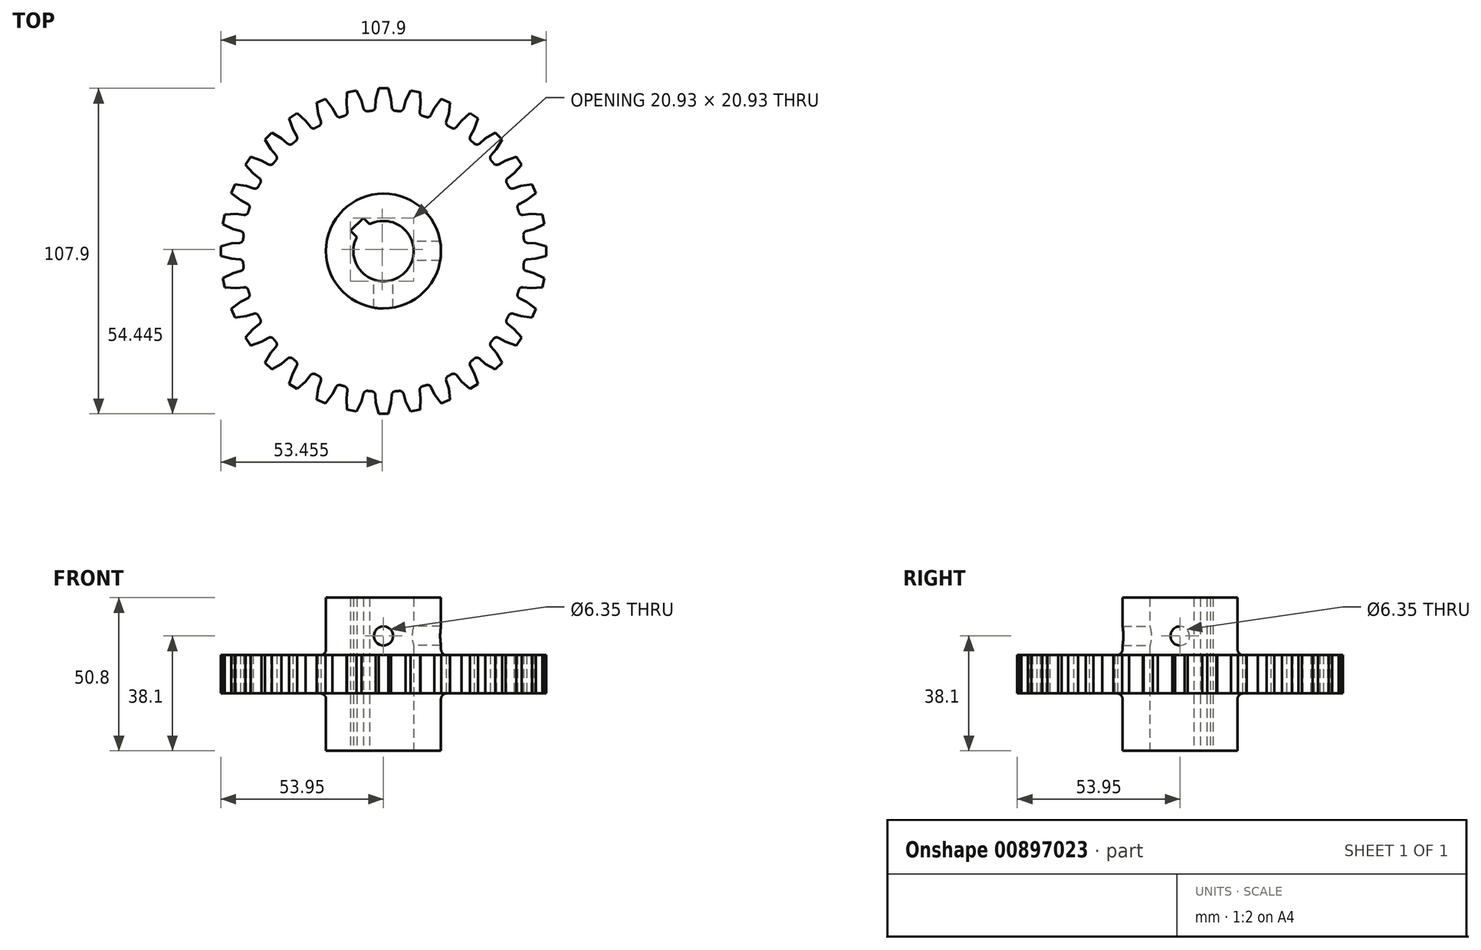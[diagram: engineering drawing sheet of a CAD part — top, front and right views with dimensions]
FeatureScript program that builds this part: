
annotation { "Feature Type Name" : "Feature", "Feature Type Description" : "" }
export const myFeature = defineFeature(function(context is Context, id is Id, definition is map)
    precondition{}
    {
        {
            var Q0;
            Q0=qCreatedBy(makeId("Top.planeOp"),FACE);
            var sketch = newSketch(context, id + "F0", { "sketchPlane" : qUnion([Q0])});
            skArc(sketch, "E0", {"start": v(-2.82, 46.59) * mm, "mid": v(-4.57, 46.45) * mm, "end": v(-6.32, 46.24) * mm});
            skLineSegment(sketch, "E1", {"start": v(1.59, 53.95) * mm, "end": v(-1.59, 53.95) * mm});
            skPoint(sketch, "E2", {"position": v(0, 53.95) * mm});
            skLineSegment(sketch, "E3", {"start": v(-1.59, 53.95) * mm, "end": v(-2.54, 50.31) * mm});
            skLineSegment(sketch, "E4", {"start": v(1.59, 53.95) * mm, "end": v(2.54, 50.31) * mm});
            skLineSegment(sketch, "E5", {"start": v(-2.54, 50.31) * mm, "end": v(-2.82, 46.59) * mm});
            skLineSegment(sketch, "E6", {"start": v(2.54, 50.31) * mm, "end": v(2.82, 46.59) * mm});
            skLineSegment(sketch, "E7.1.0", {"start": v(-8.97, 53.22) * mm, "end": v(-12.08, 52.6) * mm});
            skLineSegment(sketch, "E7.1.1", {"start": v(-7.32, 49.84) * mm, "end": v(-6.32, 46.24) * mm});
            skLineSegment(sketch, "E7.1.2", {"start": v(-8.97, 53.22) * mm, "end": v(-7.32, 49.84) * mm});
            skLineSegment(sketch, "E7.1.3", {"start": v(-12.08, 52.6) * mm, "end": v(-12.3, 48.85) * mm});
            skLineSegment(sketch, "E7.1.4", {"start": v(-12.3, 48.85) * mm, "end": v(-11.86, 45.14) * mm});
            skPoint(sketch, "E7.1.5", {"position": v(-10.53, 52.91) * mm});
            skLineSegment(sketch, "E7.2.0", {"start": v(-19.18, 50.45) * mm, "end": v(-22.11, 49.24) * mm});
            skLineSegment(sketch, "E7.2.1", {"start": v(-16.9, 47.45) * mm, "end": v(-15.22, 44.12) * mm});
            skLineSegment(sketch, "E7.2.2", {"start": v(-19.18, 50.45) * mm, "end": v(-16.9, 47.45) * mm});
            skLineSegment(sketch, "E7.2.3", {"start": v(-22.11, 49.24) * mm, "end": v(-21.6, 45.51) * mm});
            skLineSegment(sketch, "E7.2.4", {"start": v(-21.6, 45.51) * mm, "end": v(-20.44, 41.96) * mm});
            skPoint(sketch, "E7.2.5", {"position": v(-20.65, 49.84) * mm});
            skLineSegment(sketch, "E7.3.0", {"start": v(-28.65, 45.74) * mm, "end": v(-31.3, 43.98) * mm});
            skLineSegment(sketch, "E7.3.1", {"start": v(-25.84, 43.24) * mm, "end": v(-23.54, 40.3) * mm});
            skLineSegment(sketch, "E7.3.2", {"start": v(-28.65, 45.74) * mm, "end": v(-25.84, 43.24) * mm});
            skLineSegment(sketch, "E7.3.3", {"start": v(-31.3, 43.98) * mm, "end": v(-30.06, 40.42) * mm});
            skLineSegment(sketch, "E7.3.4", {"start": v(-30.06, 40.42) * mm, "end": v(-28.23, 37.17) * mm});
            skPoint(sketch, "E7.3.5", {"position": v(-29.97, 44.86) * mm});
            skLineSegment(sketch, "E7.4.0", {"start": v(-37.03, 39.27) * mm, "end": v(-39.27, 37.03) * mm});
            skLineSegment(sketch, "E7.4.1", {"start": v(-33.78, 37.37) * mm, "end": v(-30.95, 34.94) * mm});
            skLineSegment(sketch, "E7.4.2", {"start": v(-37.03, 39.27) * mm, "end": v(-33.78, 37.37) * mm});
            skLineSegment(sketch, "E7.4.3", {"start": v(-39.27, 37.03) * mm, "end": v(-37.37, 33.78) * mm});
            skLineSegment(sketch, "E7.4.4", {"start": v(-37.37, 33.78) * mm, "end": v(-34.94, 30.95) * mm});
            skPoint(sketch, "E7.4.5", {"position": v(-38.15, 38.15) * mm});
            skLineSegment(sketch, "E7.5.0", {"start": v(-43.98, 31.3) * mm, "end": v(-45.74, 28.65) * mm});
            skLineSegment(sketch, "E7.5.1", {"start": v(-40.42, 30.06) * mm, "end": v(-37.17, 28.23) * mm});
            skLineSegment(sketch, "E7.5.2", {"start": v(-43.98, 31.3) * mm, "end": v(-40.42, 30.06) * mm});
            skLineSegment(sketch, "E7.5.3", {"start": v(-45.74, 28.65) * mm, "end": v(-43.24, 25.84) * mm});
            skLineSegment(sketch, "E7.5.4", {"start": v(-43.24, 25.84) * mm, "end": v(-40.3, 23.54) * mm});
            skPoint(sketch, "E7.5.5", {"position": v(-44.86, 29.97) * mm});
            skLineSegment(sketch, "E7.6.0", {"start": v(-49.24, 22.11) * mm, "end": v(-50.45, 19.18) * mm});
            skLineSegment(sketch, "E7.6.1", {"start": v(-45.51, 21.6) * mm, "end": v(-41.96, 20.44) * mm});
            skLineSegment(sketch, "E7.6.2", {"start": v(-49.24, 22.11) * mm, "end": v(-45.51, 21.6) * mm});
            skLineSegment(sketch, "E7.6.3", {"start": v(-50.45, 19.18) * mm, "end": v(-47.45, 16.9) * mm});
            skLineSegment(sketch, "E7.6.4", {"start": v(-47.45, 16.9) * mm, "end": v(-44.12, 15.22) * mm});
            skPoint(sketch, "E7.6.5", {"position": v(-49.84, 20.65) * mm});
            skLineSegment(sketch, "E7.7.0", {"start": v(-52.6, 12.08) * mm, "end": v(-53.22, 8.97) * mm});
            skLineSegment(sketch, "E7.7.1", {"start": v(-48.85, 12.3) * mm, "end": v(-45.14, 11.86) * mm});
            skLineSegment(sketch, "E7.7.2", {"start": v(-52.6, 12.08) * mm, "end": v(-48.85, 12.3) * mm});
            skLineSegment(sketch, "E7.7.3", {"start": v(-53.22, 8.97) * mm, "end": v(-49.84, 7.32) * mm});
            skLineSegment(sketch, "E7.7.4", {"start": v(-49.84, 7.32) * mm, "end": v(-46.24, 6.32) * mm});
            skPoint(sketch, "E7.7.5", {"position": v(-52.91, 10.53) * mm});
            skLineSegment(sketch, "E7.8.0", {"start": v(-53.95, 1.59) * mm, "end": v(-53.95, -1.59) * mm});
            skLineSegment(sketch, "E7.8.1", {"start": v(-50.31, 2.54) * mm, "end": v(-46.59, 2.82) * mm});
            skLineSegment(sketch, "E7.8.2", {"start": v(-53.95, 1.59) * mm, "end": v(-50.31, 2.54) * mm});
            skLineSegment(sketch, "E7.8.3", {"start": v(-53.95, -1.59) * mm, "end": v(-50.31, -2.54) * mm});
            skLineSegment(sketch, "E7.8.4", {"start": v(-50.31, -2.54) * mm, "end": v(-46.59, -2.82) * mm});
            skPoint(sketch, "E7.8.5", {"position": v(-53.95, 0) * mm});
            skLineSegment(sketch, "E7.9.0", {"start": v(-53.22, -8.97) * mm, "end": v(-52.6, -12.08) * mm});
            skLineSegment(sketch, "E7.9.1", {"start": v(-49.84, -7.32) * mm, "end": v(-46.24, -6.32) * mm});
            skLineSegment(sketch, "E7.9.2", {"start": v(-53.22, -8.97) * mm, "end": v(-49.84, -7.32) * mm});
            skLineSegment(sketch, "E7.9.3", {"start": v(-52.6, -12.08) * mm, "end": v(-48.85, -12.3) * mm});
            skLineSegment(sketch, "E7.9.4", {"start": v(-48.85, -12.3) * mm, "end": v(-45.14, -11.86) * mm});
            skPoint(sketch, "E7.9.5", {"position": v(-52.91, -10.53) * mm});
            skLineSegment(sketch, "E7.10.0", {"start": v(-50.45, -19.18) * mm, "end": v(-49.24, -22.11) * mm});
            skLineSegment(sketch, "E7.10.1", {"start": v(-47.45, -16.9) * mm, "end": v(-44.12, -15.22) * mm});
            skLineSegment(sketch, "E7.10.2", {"start": v(-50.45, -19.18) * mm, "end": v(-47.45, -16.9) * mm});
            skLineSegment(sketch, "E7.10.3", {"start": v(-49.24, -22.11) * mm, "end": v(-45.51, -21.6) * mm});
            skLineSegment(sketch, "E7.10.4", {"start": v(-45.51, -21.6) * mm, "end": v(-41.96, -20.44) * mm});
            skPoint(sketch, "E7.10.5", {"position": v(-49.84, -20.65) * mm});
            skLineSegment(sketch, "E7.11.0", {"start": v(-45.74, -28.65) * mm, "end": v(-43.98, -31.3) * mm});
            skLineSegment(sketch, "E7.11.1", {"start": v(-43.24, -25.84) * mm, "end": v(-40.3, -23.54) * mm});
            skLineSegment(sketch, "E7.11.2", {"start": v(-45.74, -28.65) * mm, "end": v(-43.24, -25.84) * mm});
            skLineSegment(sketch, "E7.11.3", {"start": v(-43.98, -31.3) * mm, "end": v(-40.42, -30.06) * mm});
            skLineSegment(sketch, "E7.11.4", {"start": v(-40.42, -30.06) * mm, "end": v(-37.17, -28.23) * mm});
            skPoint(sketch, "E7.11.5", {"position": v(-44.86, -29.97) * mm});
            skLineSegment(sketch, "E7.12.0", {"start": v(-39.27, -37.03) * mm, "end": v(-37.03, -39.27) * mm});
            skLineSegment(sketch, "E7.12.1", {"start": v(-37.37, -33.78) * mm, "end": v(-34.94, -30.95) * mm});
            skLineSegment(sketch, "E7.12.2", {"start": v(-39.27, -37.03) * mm, "end": v(-37.37, -33.78) * mm});
            skLineSegment(sketch, "E7.12.3", {"start": v(-37.03, -39.27) * mm, "end": v(-33.78, -37.37) * mm});
            skLineSegment(sketch, "E7.12.4", {"start": v(-33.78, -37.37) * mm, "end": v(-30.95, -34.94) * mm});
            skPoint(sketch, "E7.12.5", {"position": v(-38.15, -38.15) * mm});
            skLineSegment(sketch, "E7.13.0", {"start": v(-31.3, -43.98) * mm, "end": v(-28.65, -45.74) * mm});
            skLineSegment(sketch, "E7.13.1", {"start": v(-30.06, -40.42) * mm, "end": v(-28.23, -37.17) * mm});
            skLineSegment(sketch, "E7.13.2", {"start": v(-31.3, -43.98) * mm, "end": v(-30.06, -40.42) * mm});
            skLineSegment(sketch, "E7.13.3", {"start": v(-28.65, -45.74) * mm, "end": v(-25.84, -43.24) * mm});
            skLineSegment(sketch, "E7.13.4", {"start": v(-25.84, -43.24) * mm, "end": v(-23.54, -40.3) * mm});
            skPoint(sketch, "E7.13.5", {"position": v(-29.97, -44.86) * mm});
            skLineSegment(sketch, "E7.14.0", {"start": v(-22.11, -49.24) * mm, "end": v(-19.18, -50.45) * mm});
            skLineSegment(sketch, "E7.14.1", {"start": v(-21.6, -45.51) * mm, "end": v(-20.44, -41.96) * mm});
            skLineSegment(sketch, "E7.14.2", {"start": v(-22.11, -49.24) * mm, "end": v(-21.6, -45.51) * mm});
            skLineSegment(sketch, "E7.14.3", {"start": v(-19.18, -50.45) * mm, "end": v(-16.9, -47.45) * mm});
            skLineSegment(sketch, "E7.14.4", {"start": v(-16.9, -47.45) * mm, "end": v(-15.22, -44.12) * mm});
            skPoint(sketch, "E7.14.5", {"position": v(-20.65, -49.84) * mm});
            skLineSegment(sketch, "E7.15.0", {"start": v(-12.08, -52.6) * mm, "end": v(-8.97, -53.22) * mm});
            skLineSegment(sketch, "E7.15.1", {"start": v(-12.3, -48.85) * mm, "end": v(-11.86, -45.14) * mm});
            skLineSegment(sketch, "E7.15.2", {"start": v(-12.08, -52.6) * mm, "end": v(-12.3, -48.85) * mm});
            skLineSegment(sketch, "E7.15.3", {"start": v(-8.97, -53.22) * mm, "end": v(-7.32, -49.84) * mm});
            skLineSegment(sketch, "E7.15.4", {"start": v(-7.32, -49.84) * mm, "end": v(-6.32, -46.24) * mm});
            skPoint(sketch, "E7.15.5", {"position": v(-10.53, -52.91) * mm});
            skLineSegment(sketch, "E7.16.0", {"start": v(-1.59, -53.95) * mm, "end": v(1.59, -53.95) * mm});
            skLineSegment(sketch, "E7.16.1", {"start": v(-2.54, -50.31) * mm, "end": v(-2.82, -46.59) * mm});
            skLineSegment(sketch, "E7.16.2", {"start": v(-1.59, -53.95) * mm, "end": v(-2.54, -50.31) * mm});
            skLineSegment(sketch, "E7.16.3", {"start": v(1.59, -53.95) * mm, "end": v(2.54, -50.31) * mm});
            skLineSegment(sketch, "E7.16.4", {"start": v(2.54, -50.31) * mm, "end": v(2.82, -46.59) * mm});
            skPoint(sketch, "E7.16.5", {"position": v(0, -53.95) * mm});
            skLineSegment(sketch, "E7.17.0", {"start": v(8.97, -53.22) * mm, "end": v(12.08, -52.6) * mm});
            skLineSegment(sketch, "E7.17.1", {"start": v(7.32, -49.84) * mm, "end": v(6.32, -46.24) * mm});
            skLineSegment(sketch, "E7.17.2", {"start": v(8.97, -53.22) * mm, "end": v(7.32, -49.84) * mm});
            skLineSegment(sketch, "E7.17.3", {"start": v(12.08, -52.6) * mm, "end": v(12.3, -48.85) * mm});
            skLineSegment(sketch, "E7.17.4", {"start": v(12.3, -48.85) * mm, "end": v(11.86, -45.14) * mm});
            skPoint(sketch, "E7.17.5", {"position": v(10.53, -52.91) * mm});
            skLineSegment(sketch, "E7.18.0", {"start": v(19.18, -50.45) * mm, "end": v(22.11, -49.24) * mm});
            skLineSegment(sketch, "E7.18.1", {"start": v(16.9, -47.45) * mm, "end": v(15.22, -44.12) * mm});
            skLineSegment(sketch, "E7.18.2", {"start": v(19.18, -50.45) * mm, "end": v(16.9, -47.45) * mm});
            skLineSegment(sketch, "E7.18.3", {"start": v(22.11, -49.24) * mm, "end": v(21.6, -45.51) * mm});
            skLineSegment(sketch, "E7.18.4", {"start": v(21.6, -45.51) * mm, "end": v(20.44, -41.96) * mm});
            skPoint(sketch, "E7.18.5", {"position": v(20.65, -49.84) * mm});
            skLineSegment(sketch, "E7.19.0", {"start": v(28.65, -45.74) * mm, "end": v(31.3, -43.98) * mm});
            skLineSegment(sketch, "E7.19.1", {"start": v(25.84, -43.24) * mm, "end": v(23.54, -40.3) * mm});
            skLineSegment(sketch, "E7.19.2", {"start": v(28.65, -45.74) * mm, "end": v(25.84, -43.24) * mm});
            skLineSegment(sketch, "E7.19.3", {"start": v(31.3, -43.98) * mm, "end": v(30.06, -40.42) * mm});
            skLineSegment(sketch, "E7.19.4", {"start": v(30.06, -40.42) * mm, "end": v(28.23, -37.17) * mm});
            skPoint(sketch, "E7.19.5", {"position": v(29.97, -44.86) * mm});
            skLineSegment(sketch, "E7.20.0", {"start": v(37.03, -39.27) * mm, "end": v(39.27, -37.03) * mm});
            skLineSegment(sketch, "E7.20.1", {"start": v(33.78, -37.37) * mm, "end": v(30.95, -34.94) * mm});
            skLineSegment(sketch, "E7.20.2", {"start": v(37.03, -39.27) * mm, "end": v(33.78, -37.37) * mm});
            skLineSegment(sketch, "E7.20.3", {"start": v(39.27, -37.03) * mm, "end": v(37.37, -33.78) * mm});
            skLineSegment(sketch, "E7.20.4", {"start": v(37.37, -33.78) * mm, "end": v(34.94, -30.95) * mm});
            skPoint(sketch, "E7.20.5", {"position": v(38.15, -38.15) * mm});
            skLineSegment(sketch, "E7.21.0", {"start": v(43.98, -31.3) * mm, "end": v(45.74, -28.65) * mm});
            skLineSegment(sketch, "E7.21.1", {"start": v(40.42, -30.06) * mm, "end": v(37.17, -28.23) * mm});
            skLineSegment(sketch, "E7.21.2", {"start": v(43.98, -31.3) * mm, "end": v(40.42, -30.06) * mm});
            skLineSegment(sketch, "E7.21.3", {"start": v(45.74, -28.65) * mm, "end": v(43.24, -25.84) * mm});
            skLineSegment(sketch, "E7.21.4", {"start": v(43.24, -25.84) * mm, "end": v(40.3, -23.54) * mm});
            skPoint(sketch, "E7.21.5", {"position": v(44.86, -29.97) * mm});
            skLineSegment(sketch, "E7.22.0", {"start": v(49.24, -22.11) * mm, "end": v(50.45, -19.18) * mm});
            skLineSegment(sketch, "E7.22.1", {"start": v(45.51, -21.6) * mm, "end": v(41.96, -20.44) * mm});
            skLineSegment(sketch, "E7.22.2", {"start": v(49.24, -22.11) * mm, "end": v(45.51, -21.6) * mm});
            skLineSegment(sketch, "E7.22.3", {"start": v(50.45, -19.18) * mm, "end": v(47.45, -16.9) * mm});
            skLineSegment(sketch, "E7.22.4", {"start": v(47.45, -16.9) * mm, "end": v(44.12, -15.22) * mm});
            skPoint(sketch, "E7.22.5", {"position": v(49.84, -20.65) * mm});
            skLineSegment(sketch, "E7.23.0", {"start": v(52.6, -12.08) * mm, "end": v(53.22, -8.97) * mm});
            skLineSegment(sketch, "E7.23.1", {"start": v(48.85, -12.3) * mm, "end": v(45.14, -11.86) * mm});
            skLineSegment(sketch, "E7.23.2", {"start": v(52.6, -12.08) * mm, "end": v(48.85, -12.3) * mm});
            skLineSegment(sketch, "E7.23.3", {"start": v(53.22, -8.97) * mm, "end": v(49.84, -7.32) * mm});
            skLineSegment(sketch, "E7.23.4", {"start": v(49.84, -7.32) * mm, "end": v(46.24, -6.32) * mm});
            skPoint(sketch, "E7.23.5", {"position": v(52.91, -10.53) * mm});
            skLineSegment(sketch, "E7.24.0", {"start": v(53.95, -1.59) * mm, "end": v(53.95, 1.59) * mm});
            skLineSegment(sketch, "E7.24.1", {"start": v(50.31, -2.54) * mm, "end": v(46.59, -2.82) * mm});
            skLineSegment(sketch, "E7.24.2", {"start": v(53.95, -1.59) * mm, "end": v(50.31, -2.54) * mm});
            skLineSegment(sketch, "E7.24.3", {"start": v(53.95, 1.59) * mm, "end": v(50.31, 2.54) * mm});
            skLineSegment(sketch, "E7.24.4", {"start": v(50.31, 2.54) * mm, "end": v(46.59, 2.82) * mm});
            skPoint(sketch, "E7.24.5", {"position": v(53.95, 0) * mm});
            skLineSegment(sketch, "E7.25.0", {"start": v(53.22, 8.97) * mm, "end": v(52.6, 12.08) * mm});
            skLineSegment(sketch, "E7.25.1", {"start": v(49.84, 7.32) * mm, "end": v(46.24, 6.32) * mm});
            skLineSegment(sketch, "E7.25.2", {"start": v(53.22, 8.97) * mm, "end": v(49.84, 7.32) * mm});
            skLineSegment(sketch, "E7.25.3", {"start": v(52.6, 12.08) * mm, "end": v(48.85, 12.3) * mm});
            skLineSegment(sketch, "E7.25.4", {"start": v(48.85, 12.3) * mm, "end": v(45.14, 11.86) * mm});
            skPoint(sketch, "E7.25.5", {"position": v(52.91, 10.53) * mm});
            skLineSegment(sketch, "E7.26.0", {"start": v(50.45, 19.18) * mm, "end": v(49.24, 22.11) * mm});
            skLineSegment(sketch, "E7.26.1", {"start": v(47.45, 16.9) * mm, "end": v(44.12, 15.22) * mm});
            skLineSegment(sketch, "E7.26.2", {"start": v(50.45, 19.18) * mm, "end": v(47.45, 16.9) * mm});
            skLineSegment(sketch, "E7.26.3", {"start": v(49.24, 22.11) * mm, "end": v(45.51, 21.6) * mm});
            skLineSegment(sketch, "E7.26.4", {"start": v(45.51, 21.6) * mm, "end": v(41.96, 20.44) * mm});
            skPoint(sketch, "E7.26.5", {"position": v(49.84, 20.65) * mm});
            skLineSegment(sketch, "E7.27.0", {"start": v(45.74, 28.65) * mm, "end": v(43.98, 31.3) * mm});
            skLineSegment(sketch, "E7.27.1", {"start": v(43.24, 25.84) * mm, "end": v(40.3, 23.54) * mm});
            skLineSegment(sketch, "E7.27.2", {"start": v(45.74, 28.65) * mm, "end": v(43.24, 25.84) * mm});
            skLineSegment(sketch, "E7.27.3", {"start": v(43.98, 31.3) * mm, "end": v(40.42, 30.06) * mm});
            skLineSegment(sketch, "E7.27.4", {"start": v(40.42, 30.06) * mm, "end": v(37.17, 28.23) * mm});
            skPoint(sketch, "E7.27.5", {"position": v(44.86, 29.97) * mm});
            skLineSegment(sketch, "E7.28.0", {"start": v(39.27, 37.03) * mm, "end": v(37.03, 39.27) * mm});
            skLineSegment(sketch, "E7.28.1", {"start": v(37.37, 33.78) * mm, "end": v(34.94, 30.95) * mm});
            skLineSegment(sketch, "E7.28.2", {"start": v(39.27, 37.03) * mm, "end": v(37.37, 33.78) * mm});
            skLineSegment(sketch, "E7.28.3", {"start": v(37.03, 39.27) * mm, "end": v(33.78, 37.37) * mm});
            skLineSegment(sketch, "E7.28.4", {"start": v(33.78, 37.37) * mm, "end": v(30.95, 34.94) * mm});
            skPoint(sketch, "E7.28.5", {"position": v(38.15, 38.15) * mm});
            skLineSegment(sketch, "E7.29.0", {"start": v(31.3, 43.98) * mm, "end": v(28.65, 45.74) * mm});
            skLineSegment(sketch, "E7.29.1", {"start": v(30.06, 40.42) * mm, "end": v(28.23, 37.17) * mm});
            skLineSegment(sketch, "E7.29.2", {"start": v(31.3, 43.98) * mm, "end": v(30.06, 40.42) * mm});
            skLineSegment(sketch, "E7.29.3", {"start": v(28.65, 45.74) * mm, "end": v(25.84, 43.24) * mm});
            skLineSegment(sketch, "E7.29.4", {"start": v(25.84, 43.24) * mm, "end": v(23.54, 40.3) * mm});
            skPoint(sketch, "E7.29.5", {"position": v(29.97, 44.86) * mm});
            skLineSegment(sketch, "E7.30.0", {"start": v(22.11, 49.24) * mm, "end": v(19.18, 50.45) * mm});
            skLineSegment(sketch, "E7.30.1", {"start": v(21.6, 45.51) * mm, "end": v(20.44, 41.96) * mm});
            skLineSegment(sketch, "E7.30.2", {"start": v(22.11, 49.24) * mm, "end": v(21.6, 45.51) * mm});
            skLineSegment(sketch, "E7.30.3", {"start": v(19.18, 50.45) * mm, "end": v(16.9, 47.45) * mm});
            skLineSegment(sketch, "E7.30.4", {"start": v(16.9, 47.45) * mm, "end": v(15.22, 44.12) * mm});
            skPoint(sketch, "E7.30.5", {"position": v(20.65, 49.84) * mm});
            skLineSegment(sketch, "E7.31.0", {"start": v(12.08, 52.6) * mm, "end": v(8.97, 53.22) * mm});
            skLineSegment(sketch, "E7.31.1", {"start": v(12.3, 48.85) * mm, "end": v(11.86, 45.14) * mm});
            skLineSegment(sketch, "E7.31.2", {"start": v(12.08, 52.6) * mm, "end": v(12.3, 48.85) * mm});
            skLineSegment(sketch, "E7.31.3", {"start": v(8.97, 53.22) * mm, "end": v(7.32, 49.84) * mm});
            skLineSegment(sketch, "E7.31.4", {"start": v(7.32, 49.84) * mm, "end": v(6.32, 46.24) * mm});
            skPoint(sketch, "E7.31.5", {"position": v(10.53, 52.91) * mm});
            skArc(sketch, "E8.trimOffspring", {"start": v(6.32, 46.24) * mm, "mid": v(4.57, 46.45) * mm, "end": v(2.82, 46.59) * mm});
            skArc(sketch, "E9.trimOffspring", {"start": v(15.22, 44.12) * mm, "mid": v(13.55, 44.66) * mm, "end": v(11.86, 45.14) * mm});
            skArc(sketch, "E10.trimOffspring", {"start": v(23.54, 40.3) * mm, "mid": v(22, 41.16) * mm, "end": v(20.44, 41.96) * mm});
            skArc(sketch, "E11.trimOffspring", {"start": v(30.95, 34.94) * mm, "mid": v(29.6, 36.08) * mm, "end": v(28.23, 37.17) * mm});
            skArc(sketch, "E12.trimOffspring", {"start": v(37.17, 28.23) * mm, "mid": v(36.08, 29.6) * mm, "end": v(34.94, 30.95) * mm});
            skArc(sketch, "E13.trimOffspring", {"start": v(41.96, 20.44) * mm, "mid": v(41.16, 22) * mm, "end": v(40.3, 23.54) * mm});
            skArc(sketch, "E14.trimOffspring", {"start": v(45.14, 11.86) * mm, "mid": v(44.66, 13.55) * mm, "end": v(44.12, 15.22) * mm});
            skArc(sketch, "E15.trimOffspring", {"start": v(46.59, 2.82) * mm, "mid": v(46.45, 4.57) * mm, "end": v(46.24, 6.32) * mm});
            skArc(sketch, "E16.trimOffspring", {"start": v(46.24, -6.32) * mm, "mid": v(46.45, -4.57) * mm, "end": v(46.59, -2.82) * mm});
            skArc(sketch, "E17.trimOffspring", {"start": v(44.12, -15.22) * mm, "mid": v(44.66, -13.55) * mm, "end": v(45.14, -11.86) * mm});
            skArc(sketch, "E18.trimOffspring", {"start": v(40.3, -23.54) * mm, "mid": v(41.16, -22) * mm, "end": v(41.96, -20.44) * mm});
            skArc(sketch, "E19.trimOffspring", {"start": v(34.94, -30.95) * mm, "mid": v(36.08, -29.6) * mm, "end": v(37.17, -28.23) * mm});
            skArc(sketch, "E20.trimOffspring", {"start": v(28.23, -37.17) * mm, "mid": v(29.6, -36.08) * mm, "end": v(30.95, -34.94) * mm});
            skArc(sketch, "E21.trimOffspring", {"start": v(20.44, -41.96) * mm, "mid": v(22, -41.16) * mm, "end": v(23.54, -40.3) * mm});
            skArc(sketch, "E22.trimOffspring", {"start": v(11.86, -45.14) * mm, "mid": v(13.55, -44.66) * mm, "end": v(15.22, -44.12) * mm});
            skArc(sketch, "E23.trimOffspring", {"start": v(2.82, -46.59) * mm, "mid": v(4.57, -46.45) * mm, "end": v(6.32, -46.24) * mm});
            skArc(sketch, "E24.trimOffspring", {"start": v(-6.32, -46.24) * mm, "mid": v(-4.57, -46.45) * mm, "end": v(-2.82, -46.59) * mm});
            skArc(sketch, "E25.trimOffspring", {"start": v(-15.22, -44.12) * mm, "mid": v(-13.55, -44.66) * mm, "end": v(-11.86, -45.14) * mm});
            skArc(sketch, "E26.trimOffspring", {"start": v(-23.54, -40.3) * mm, "mid": v(-22, -41.16) * mm, "end": v(-20.44, -41.96) * mm});
            skArc(sketch, "E27.trimOffspring", {"start": v(-30.95, -34.94) * mm, "mid": v(-29.6, -36.08) * mm, "end": v(-28.23, -37.17) * mm});
            skArc(sketch, "E28.trimOffspring", {"start": v(-37.17, -28.23) * mm, "mid": v(-36.08, -29.6) * mm, "end": v(-34.94, -30.95) * mm});
            skArc(sketch, "E29.trimOffspring", {"start": v(-41.96, -20.44) * mm, "mid": v(-41.16, -22) * mm, "end": v(-40.3, -23.54) * mm});
            skArc(sketch, "E30.trimOffspring", {"start": v(-45.14, -11.86) * mm, "mid": v(-44.66, -13.55) * mm, "end": v(-44.12, -15.22) * mm});
            skArc(sketch, "E31.trimOffspring", {"start": v(-46.59, -2.82) * mm, "mid": v(-46.45, -4.57) * mm, "end": v(-46.24, -6.32) * mm});
            skArc(sketch, "E32.trimOffspring", {"start": v(-46.24, 6.32) * mm, "mid": v(-46.45, 4.57) * mm, "end": v(-46.59, 2.82) * mm});
            skArc(sketch, "E33.trimOffspring", {"start": v(-44.12, 15.22) * mm, "mid": v(-44.66, 13.55) * mm, "end": v(-45.14, 11.86) * mm});
            skArc(sketch, "E34.trimOffspring", {"start": v(-40.3, 23.54) * mm, "mid": v(-41.16, 22) * mm, "end": v(-41.96, 20.44) * mm});
            skArc(sketch, "E35.trimOffspring", {"start": v(-34.94, 30.95) * mm, "mid": v(-36.08, 29.6) * mm, "end": v(-37.17, 28.23) * mm});
            skArc(sketch, "E36.trimOffspring", {"start": v(-28.23, 37.17) * mm, "mid": v(-29.6, 36.08) * mm, "end": v(-30.95, 34.94) * mm});
            skArc(sketch, "E37.trimOffspring", {"start": v(-20.44, 41.96) * mm, "mid": v(-22, 41.16) * mm, "end": v(-23.54, 40.3) * mm});
            skArc(sketch, "E38.trimOffspring", {"start": v(-11.86, 45.14) * mm, "mid": v(-13.55, 44.66) * mm, "end": v(-15.22, 44.12) * mm});
            skSolve(sketch);
        }
        {
            var Q0;
            Q0=makeQuery(id+"F0.imprint","IMPRINT",FACE,{"disambiguationData":[TD([[makeQuery(id+"F0.imprint","IMPRINT",EDGE,{"derivedFrom":sQuery(id+"F0.wireOp",EDGE,"E0")}),1.0]])]});
            extrude(context, id + "F1", {"entities" : qUnion([Q0]), "depth" : 12.7 * mm, "offsetDistance" : 25.4 * mm});
        }
        {
            var Q0;
            Q0=makeQuery(id+"F1.opExtrude","SWEPT_EDGE",EDGE,{"disambiguationData":[OSD([sQuery(id+"F0.wireOp",EDGE,"E6"),sQuery(id+"F0.wireOp",EDGE,"E8.trimOffspring")])]});
            var Q1;
            Q1=makeQuery(id+"F1.opExtrude","SWEPT_EDGE",EDGE,{"disambiguationData":[OSD([sQuery(id+"F0.wireOp",EDGE,"E7.31.4"),sQuery(id+"F0.wireOp",EDGE,"E8.trimOffspring")])]});
            var Q2;
            Q2=makeQuery(id+"F1.opExtrude","SWEPT_EDGE",EDGE,{"disambiguationData":[OSD([sQuery(id+"F0.wireOp",EDGE,"E7.31.1"),sQuery(id+"F0.wireOp",EDGE,"E9.trimOffspring")])]});
            var Q3;
            Q3=makeQuery(id+"F1.opExtrude","SWEPT_EDGE",EDGE,{"disambiguationData":[OSD([sQuery(id+"F0.wireOp",EDGE,"E7.30.4"),sQuery(id+"F0.wireOp",EDGE,"E9.trimOffspring")])]});
            var Q4;
            Q4=makeQuery(id+"F1.opExtrude","SWEPT_EDGE",EDGE,{"disambiguationData":[OSD([sQuery(id+"F0.wireOp",EDGE,"E7.30.1"),sQuery(id+"F0.wireOp",EDGE,"E10.trimOffspring")])]});
            var Q5;
            Q5=makeQuery(id+"F1.opExtrude","SWEPT_EDGE",EDGE,{"disambiguationData":[OSD([sQuery(id+"F0.wireOp",EDGE,"E7.29.4"),sQuery(id+"F0.wireOp",EDGE,"E10.trimOffspring")])]});
            var Q6;
            Q6=makeQuery(id+"F1.opExtrude","SWEPT_EDGE",EDGE,{"disambiguationData":[OSD([sQuery(id+"F0.wireOp",EDGE,"E7.29.1"),sQuery(id+"F0.wireOp",EDGE,"E11.trimOffspring")])]});
            var Q7;
            Q7=makeQuery(id+"F1.opExtrude","SWEPT_EDGE",EDGE,{"disambiguationData":[OSD([sQuery(id+"F0.wireOp",EDGE,"E7.28.4"),sQuery(id+"F0.wireOp",EDGE,"E11.trimOffspring")])]});
            var Q8;
            Q8=makeQuery(id+"F1.opExtrude","SWEPT_EDGE",EDGE,{"disambiguationData":[OSD([sQuery(id+"F0.wireOp",EDGE,"E7.28.1"),sQuery(id+"F0.wireOp",EDGE,"E12.trimOffspring")])]});
            var Q9;
            Q9=makeQuery(id+"F1.opExtrude","SWEPT_EDGE",EDGE,{"disambiguationData":[OSD([sQuery(id+"F0.wireOp",EDGE,"E7.27.4"),sQuery(id+"F0.wireOp",EDGE,"E12.trimOffspring")])]});
            var Q10;
            Q10=makeQuery(id+"F1.opExtrude","SWEPT_EDGE",EDGE,{"disambiguationData":[OSD([sQuery(id+"F0.wireOp",EDGE,"E7.27.1"),sQuery(id+"F0.wireOp",EDGE,"E13.trimOffspring")])]});
            var Q11;
            Q11=makeQuery(id+"F1.opExtrude","SWEPT_EDGE",EDGE,{"disambiguationData":[OSD([sQuery(id+"F0.wireOp",EDGE,"E7.26.4"),sQuery(id+"F0.wireOp",EDGE,"E13.trimOffspring")])]});
            var Q12;
            Q12=makeQuery(id+"F1.opExtrude","SWEPT_EDGE",EDGE,{"disambiguationData":[OSD([sQuery(id+"F0.wireOp",EDGE,"E7.26.1"),sQuery(id+"F0.wireOp",EDGE,"E14.trimOffspring")])]});
            var Q13;
            Q13=makeQuery(id+"F1.opExtrude","SWEPT_EDGE",EDGE,{"disambiguationData":[OSD([sQuery(id+"F0.wireOp",EDGE,"E7.25.4"),sQuery(id+"F0.wireOp",EDGE,"E14.trimOffspring")])]});
            var Q14;
            Q14=makeQuery(id+"F1.opExtrude","SWEPT_EDGE",EDGE,{"disambiguationData":[OSD([sQuery(id+"F0.wireOp",EDGE,"E7.25.1"),sQuery(id+"F0.wireOp",EDGE,"E15.trimOffspring")])]});
            var Q15;
            Q15=makeQuery(id+"F1.opExtrude","SWEPT_EDGE",EDGE,{"disambiguationData":[OSD([sQuery(id+"F0.wireOp",EDGE,"E7.24.4"),sQuery(id+"F0.wireOp",EDGE,"E15.trimOffspring")])]});
            var Q16;
            Q16=makeQuery(id+"F1.opExtrude","SWEPT_EDGE",EDGE,{"disambiguationData":[OSD([sQuery(id+"F0.wireOp",EDGE,"E7.24.1"),sQuery(id+"F0.wireOp",EDGE,"E16.trimOffspring")])]});
            var Q17;
            Q17=makeQuery(id+"F1.opExtrude","SWEPT_EDGE",EDGE,{"disambiguationData":[OSD([sQuery(id+"F0.wireOp",EDGE,"E7.23.4"),sQuery(id+"F0.wireOp",EDGE,"E16.trimOffspring")])]});
            var Q18;
            Q18=makeQuery(id+"F1.opExtrude","SWEPT_EDGE",EDGE,{"disambiguationData":[OSD([sQuery(id+"F0.wireOp",EDGE,"E7.23.1"),sQuery(id+"F0.wireOp",EDGE,"E17.trimOffspring")])]});
            var Q19;
            Q19=makeQuery(id+"F1.opExtrude","SWEPT_EDGE",EDGE,{"disambiguationData":[OSD([sQuery(id+"F0.wireOp",EDGE,"E7.22.4"),sQuery(id+"F0.wireOp",EDGE,"E17.trimOffspring")])]});
            var Q20;
            Q20=makeQuery(id+"F1.opExtrude","SWEPT_EDGE",EDGE,{"disambiguationData":[OSD([sQuery(id+"F0.wireOp",EDGE,"E7.22.1"),sQuery(id+"F0.wireOp",EDGE,"E18.trimOffspring")])]});
            var Q21;
            Q21=makeQuery(id+"F1.opExtrude","SWEPT_EDGE",EDGE,{"disambiguationData":[OSD([sQuery(id+"F0.wireOp",EDGE,"E7.21.4"),sQuery(id+"F0.wireOp",EDGE,"E18.trimOffspring")])]});
            var Q22;
            Q22=makeQuery(id+"F1.opExtrude","SWEPT_EDGE",EDGE,{"disambiguationData":[OSD([sQuery(id+"F0.wireOp",EDGE,"E7.21.1"),sQuery(id+"F0.wireOp",EDGE,"E19.trimOffspring")])]});
            var Q23;
            Q23=makeQuery(id+"F1.opExtrude","SWEPT_EDGE",EDGE,{"disambiguationData":[OSD([sQuery(id+"F0.wireOp",EDGE,"E7.20.4"),sQuery(id+"F0.wireOp",EDGE,"E19.trimOffspring")])]});
            var Q24;
            Q24=makeQuery(id+"F1.opExtrude","SWEPT_EDGE",EDGE,{"disambiguationData":[OSD([sQuery(id+"F0.wireOp",EDGE,"E7.20.1"),sQuery(id+"F0.wireOp",EDGE,"E20.trimOffspring")])]});
            var Q25;
            Q25=makeQuery(id+"F1.opExtrude","SWEPT_EDGE",EDGE,{"disambiguationData":[OSD([sQuery(id+"F0.wireOp",EDGE,"E7.19.4"),sQuery(id+"F0.wireOp",EDGE,"E20.trimOffspring")])]});
            var Q26;
            Q26=makeQuery(id+"F1.opExtrude","SWEPT_EDGE",EDGE,{"disambiguationData":[OSD([sQuery(id+"F0.wireOp",EDGE,"E7.19.1"),sQuery(id+"F0.wireOp",EDGE,"E21.trimOffspring")])]});
            var Q27;
            Q27=makeQuery(id+"F1.opExtrude","SWEPT_EDGE",EDGE,{"disambiguationData":[OSD([sQuery(id+"F0.wireOp",EDGE,"E7.18.4"),sQuery(id+"F0.wireOp",EDGE,"E21.trimOffspring")])]});
            var Q28;
            Q28=makeQuery(id+"F1.opExtrude","SWEPT_EDGE",EDGE,{"disambiguationData":[OSD([sQuery(id+"F0.wireOp",EDGE,"E7.18.1"),sQuery(id+"F0.wireOp",EDGE,"E22.trimOffspring")])]});
            var Q29;
            Q29=makeQuery(id+"F1.opExtrude","SWEPT_EDGE",EDGE,{"disambiguationData":[OSD([sQuery(id+"F0.wireOp",EDGE,"E7.17.4"),sQuery(id+"F0.wireOp",EDGE,"E22.trimOffspring")])]});
            var Q30;
            Q30=makeQuery(id+"F1.opExtrude","SWEPT_EDGE",EDGE,{"disambiguationData":[OSD([sQuery(id+"F0.wireOp",EDGE,"E7.17.1"),sQuery(id+"F0.wireOp",EDGE,"E23.trimOffspring")])]});
            var Q31;
            Q31=makeQuery(id+"F1.opExtrude","SWEPT_EDGE",EDGE,{"disambiguationData":[OSD([sQuery(id+"F0.wireOp",EDGE,"E7.16.4"),sQuery(id+"F0.wireOp",EDGE,"E23.trimOffspring")])]});
            var Q32;
            Q32=makeQuery(id+"F1.opExtrude","SWEPT_EDGE",EDGE,{"disambiguationData":[OSD([sQuery(id+"F0.wireOp",EDGE,"E7.16.1"),sQuery(id+"F0.wireOp",EDGE,"E24.trimOffspring")])]});
            var Q33;
            Q33=makeQuery(id+"F1.opExtrude","SWEPT_EDGE",EDGE,{"disambiguationData":[OSD([sQuery(id+"F0.wireOp",EDGE,"E7.15.4"),sQuery(id+"F0.wireOp",EDGE,"E24.trimOffspring")])]});
            var Q34;
            Q34=makeQuery(id+"F1.opExtrude","SWEPT_EDGE",EDGE,{"disambiguationData":[OSD([sQuery(id+"F0.wireOp",EDGE,"E7.15.1"),sQuery(id+"F0.wireOp",EDGE,"E25.trimOffspring")])]});
            var Q35;
            Q35=makeQuery(id+"F1.opExtrude","SWEPT_EDGE",EDGE,{"disambiguationData":[OSD([sQuery(id+"F0.wireOp",EDGE,"E7.14.4"),sQuery(id+"F0.wireOp",EDGE,"E25.trimOffspring")])]});
            var Q36;
            Q36=makeQuery(id+"F1.opExtrude","SWEPT_EDGE",EDGE,{"disambiguationData":[OSD([sQuery(id+"F0.wireOp",EDGE,"E7.14.1"),sQuery(id+"F0.wireOp",EDGE,"E26.trimOffspring")])]});
            var Q37;
            Q37=makeQuery(id+"F1.opExtrude","SWEPT_EDGE",EDGE,{"disambiguationData":[OSD([sQuery(id+"F0.wireOp",EDGE,"E7.13.4"),sQuery(id+"F0.wireOp",EDGE,"E26.trimOffspring")])]});
            var Q38;
            Q38=makeQuery(id+"F1.opExtrude","SWEPT_EDGE",EDGE,{"disambiguationData":[OSD([sQuery(id+"F0.wireOp",EDGE,"E7.13.1"),sQuery(id+"F0.wireOp",EDGE,"E27.trimOffspring")])]});
            var Q39;
            Q39=makeQuery(id+"F1.opExtrude","SWEPT_EDGE",EDGE,{"disambiguationData":[OSD([sQuery(id+"F0.wireOp",EDGE,"E7.12.4"),sQuery(id+"F0.wireOp",EDGE,"E27.trimOffspring")])]});
            var Q40;
            Q40=makeQuery(id+"F1.opExtrude","SWEPT_EDGE",EDGE,{"disambiguationData":[OSD([sQuery(id+"F0.wireOp",EDGE,"E7.12.1"),sQuery(id+"F0.wireOp",EDGE,"E28.trimOffspring")])]});
            var Q41;
            Q41=makeQuery(id+"F1.opExtrude","SWEPT_EDGE",EDGE,{"disambiguationData":[OSD([sQuery(id+"F0.wireOp",EDGE,"E7.11.4"),sQuery(id+"F0.wireOp",EDGE,"E28.trimOffspring")])]});
            var Q42;
            Q42=makeQuery(id+"F1.opExtrude","SWEPT_EDGE",EDGE,{"disambiguationData":[OSD([sQuery(id+"F0.wireOp",EDGE,"E7.11.1"),sQuery(id+"F0.wireOp",EDGE,"E29.trimOffspring")])]});
            var Q43;
            Q43=makeQuery(id+"F1.opExtrude","SWEPT_EDGE",EDGE,{"disambiguationData":[OSD([sQuery(id+"F0.wireOp",EDGE,"E7.10.4"),sQuery(id+"F0.wireOp",EDGE,"E29.trimOffspring")])]});
            var Q44;
            Q44=makeQuery(id+"F1.opExtrude","SWEPT_EDGE",EDGE,{"disambiguationData":[OSD([sQuery(id+"F0.wireOp",EDGE,"E7.10.1"),sQuery(id+"F0.wireOp",EDGE,"E30.trimOffspring")])]});
            var Q45;
            Q45=makeQuery(id+"F1.opExtrude","SWEPT_EDGE",EDGE,{"disambiguationData":[OSD([sQuery(id+"F0.wireOp",EDGE,"E7.9.4"),sQuery(id+"F0.wireOp",EDGE,"E30.trimOffspring")])]});
            var Q46;
            Q46=makeQuery(id+"F1.opExtrude","SWEPT_EDGE",EDGE,{"disambiguationData":[OSD([sQuery(id+"F0.wireOp",EDGE,"E7.9.1"),sQuery(id+"F0.wireOp",EDGE,"E31.trimOffspring")])]});
            var Q47;
            Q47=makeQuery(id+"F1.opExtrude","SWEPT_EDGE",EDGE,{"disambiguationData":[OSD([sQuery(id+"F0.wireOp",EDGE,"E7.8.4"),sQuery(id+"F0.wireOp",EDGE,"E31.trimOffspring")])]});
            var Q48;
            Q48=makeQuery(id+"F1.opExtrude","SWEPT_EDGE",EDGE,{"disambiguationData":[OSD([sQuery(id+"F0.wireOp",EDGE,"E7.8.1"),sQuery(id+"F0.wireOp",EDGE,"E32.trimOffspring")])]});
            var Q49;
            Q49=makeQuery(id+"F1.opExtrude","SWEPT_EDGE",EDGE,{"disambiguationData":[OSD([sQuery(id+"F0.wireOp",EDGE,"E7.7.4"),sQuery(id+"F0.wireOp",EDGE,"E32.trimOffspring")])]});
            var Q50;
            Q50=makeQuery(id+"F1.opExtrude","SWEPT_EDGE",EDGE,{"disambiguationData":[OSD([sQuery(id+"F0.wireOp",EDGE,"E7.7.1"),sQuery(id+"F0.wireOp",EDGE,"E33.trimOffspring")])]});
            var Q51;
            Q51=makeQuery(id+"F1.opExtrude","SWEPT_EDGE",EDGE,{"disambiguationData":[OSD([sQuery(id+"F0.wireOp",EDGE,"E7.6.4"),sQuery(id+"F0.wireOp",EDGE,"E33.trimOffspring")])]});
            var Q52;
            Q52=makeQuery(id+"F1.opExtrude","SWEPT_EDGE",EDGE,{"disambiguationData":[OSD([sQuery(id+"F0.wireOp",EDGE,"E7.6.1"),sQuery(id+"F0.wireOp",EDGE,"E34.trimOffspring")])]});
            var Q53;
            Q53=makeQuery(id+"F1.opExtrude","SWEPT_EDGE",EDGE,{"disambiguationData":[OSD([sQuery(id+"F0.wireOp",EDGE,"E7.5.4"),sQuery(id+"F0.wireOp",EDGE,"E34.trimOffspring")])]});
            var Q54;
            Q54=makeQuery(id+"F1.opExtrude","SWEPT_EDGE",EDGE,{"disambiguationData":[OSD([sQuery(id+"F0.wireOp",EDGE,"E7.5.1"),sQuery(id+"F0.wireOp",EDGE,"E35.trimOffspring")])]});
            var Q55;
            Q55=makeQuery(id+"F1.opExtrude","SWEPT_EDGE",EDGE,{"disambiguationData":[OSD([sQuery(id+"F0.wireOp",EDGE,"E7.4.4"),sQuery(id+"F0.wireOp",EDGE,"E35.trimOffspring")])]});
            var Q56;
            Q56=makeQuery(id+"F1.opExtrude","SWEPT_EDGE",EDGE,{"disambiguationData":[OSD([sQuery(id+"F0.wireOp",EDGE,"E7.4.1"),sQuery(id+"F0.wireOp",EDGE,"E36.trimOffspring")])]});
            var Q57;
            Q57=makeQuery(id+"F1.opExtrude","SWEPT_EDGE",EDGE,{"disambiguationData":[OSD([sQuery(id+"F0.wireOp",EDGE,"E7.3.4"),sQuery(id+"F0.wireOp",EDGE,"E36.trimOffspring")])]});
            var Q58;
            Q58=makeQuery(id+"F1.opExtrude","SWEPT_EDGE",EDGE,{"disambiguationData":[OSD([sQuery(id+"F0.wireOp",EDGE,"E7.3.1"),sQuery(id+"F0.wireOp",EDGE,"E37.trimOffspring")])]});
            var Q59;
            Q59=makeQuery(id+"F1.opExtrude","SWEPT_EDGE",EDGE,{"disambiguationData":[OSD([sQuery(id+"F0.wireOp",EDGE,"E7.2.4"),sQuery(id+"F0.wireOp",EDGE,"E37.trimOffspring")])]});
            var Q60;
            Q60=makeQuery(id+"F1.opExtrude","SWEPT_EDGE",EDGE,{"disambiguationData":[OSD([sQuery(id+"F0.wireOp",EDGE,"E7.2.1"),sQuery(id+"F0.wireOp",EDGE,"E38.trimOffspring")])]});
            var Q61;
            Q61=makeQuery(id+"F1.opExtrude","SWEPT_EDGE",EDGE,{"disambiguationData":[OSD([sQuery(id+"F0.wireOp",EDGE,"E7.1.4"),sQuery(id+"F0.wireOp",EDGE,"E38.trimOffspring")])]});
            var Q62;
            Q62=makeQuery(id+"F1.opExtrude","SWEPT_EDGE",EDGE,{"disambiguationData":[OSD([sQuery(id+"F0.wireOp",EDGE,"E0"),sQuery(id+"F0.wireOp",EDGE,"E7.1.1")])]});
            var Q63;
            Q63=makeQuery(id+"F1.opExtrude","SWEPT_EDGE",EDGE,{"disambiguationData":[OSD([sQuery(id+"F0.wireOp",EDGE,"E0"),sQuery(id+"F0.wireOp",EDGE,"E5")])]});
            fillet(context, id + "F2", {"entities" : qUnion([Q0, Q1, Q2, Q3, Q4, Q5, Q6, Q7, Q8, Q9, Q10, Q11, Q12, Q13, Q14, Q15, Q16, Q17, Q18, Q19, Q20, Q21, Q22, Q23, Q24, Q25, Q26, Q27, Q28, Q29, Q30, Q31, Q32, Q33, Q34, Q35, Q36, Q37, Q38, Q39, Q40, Q41, Q42, Q43, Q44, Q45, Q46, Q47, Q48, Q49, Q50, Q51, Q52, Q53, Q54, Q55, Q56, Q57, Q58, Q59, Q60, Q61, Q62, Q63]), "radius" : 1.27 * mm, "tangentPropagation" : true, "allowEdgeOverflow" : false});
        }
        {
            var Q0;
            Q0=makeQuery(id+"F1.opExtrude","CAP_FACE",FACE,{"disambiguationData":[OSD([sQuery(id+"F0.wireOp",EDGE,"E0"),sQuery(id+"F0.wireOp",EDGE,"E1"),sQuery(id+"F0.wireOp",EDGE,"E3"),sQuery(id+"F0.wireOp",EDGE,"E4"),sQuery(id+"F0.wireOp",EDGE,"E5"),sQuery(id+"F0.wireOp",EDGE,"E6"),sQuery(id+"F0.wireOp",EDGE,"E7.1.0"),sQuery(id+"F0.wireOp",EDGE,"E7.1.1"),sQuery(id+"F0.wireOp",EDGE,"E7.1.2"),sQuery(id+"F0.wireOp",EDGE,"E7.1.3"),sQuery(id+"F0.wireOp",EDGE,"E7.1.4"),sQuery(id+"F0.wireOp",EDGE,"E7.2.0"),sQuery(id+"F0.wireOp",EDGE,"E7.2.1"),sQuery(id+"F0.wireOp",EDGE,"E7.2.2"),sQuery(id+"F0.wireOp",EDGE,"E7.2.3"),sQuery(id+"F0.wireOp",EDGE,"E7.2.4"),sQuery(id+"F0.wireOp",EDGE,"E7.3.0"),sQuery(id+"F0.wireOp",EDGE,"E7.3.1"),sQuery(id+"F0.wireOp",EDGE,"E7.3.2"),sQuery(id+"F0.wireOp",EDGE,"E7.3.3"),sQuery(id+"F0.wireOp",EDGE,"E7.3.4"),sQuery(id+"F0.wireOp",EDGE,"E7.4.0"),sQuery(id+"F0.wireOp",EDGE,"E7.4.1"),sQuery(id+"F0.wireOp",EDGE,"E7.4.2"),sQuery(id+"F0.wireOp",EDGE,"E7.4.3"),sQuery(id+"F0.wireOp",EDGE,"E7.4.4"),sQuery(id+"F0.wireOp",EDGE,"E7.5.0"),sQuery(id+"F0.wireOp",EDGE,"E7.5.1"),sQuery(id+"F0.wireOp",EDGE,"E7.5.2"),sQuery(id+"F0.wireOp",EDGE,"E7.5.3"),sQuery(id+"F0.wireOp",EDGE,"E7.5.4"),sQuery(id+"F0.wireOp",EDGE,"E7.6.0"),sQuery(id+"F0.wireOp",EDGE,"E7.6.1"),sQuery(id+"F0.wireOp",EDGE,"E7.6.2"),sQuery(id+"F0.wireOp",EDGE,"E7.6.3"),sQuery(id+"F0.wireOp",EDGE,"E7.6.4"),sQuery(id+"F0.wireOp",EDGE,"E7.7.0"),sQuery(id+"F0.wireOp",EDGE,"E7.7.1"),sQuery(id+"F0.wireOp",EDGE,"E7.7.2"),sQuery(id+"F0.wireOp",EDGE,"E7.7.3"),sQuery(id+"F0.wireOp",EDGE,"E7.7.4"),sQuery(id+"F0.wireOp",EDGE,"E7.8.0"),sQuery(id+"F0.wireOp",EDGE,"E7.8.1"),sQuery(id+"F0.wireOp",EDGE,"E7.8.2"),sQuery(id+"F0.wireOp",EDGE,"E7.8.3"),sQuery(id+"F0.wireOp",EDGE,"E7.8.4"),sQuery(id+"F0.wireOp",EDGE,"E7.9.0"),sQuery(id+"F0.wireOp",EDGE,"E7.9.1"),sQuery(id+"F0.wireOp",EDGE,"E7.9.2"),sQuery(id+"F0.wireOp",EDGE,"E7.9.3"),sQuery(id+"F0.wireOp",EDGE,"E7.9.4"),sQuery(id+"F0.wireOp",EDGE,"E7.10.0"),sQuery(id+"F0.wireOp",EDGE,"E7.10.1"),sQuery(id+"F0.wireOp",EDGE,"E7.10.2"),sQuery(id+"F0.wireOp",EDGE,"E7.10.3"),sQuery(id+"F0.wireOp",EDGE,"E7.10.4"),sQuery(id+"F0.wireOp",EDGE,"E7.11.0"),sQuery(id+"F0.wireOp",EDGE,"E7.11.1"),sQuery(id+"F0.wireOp",EDGE,"E7.11.2"),sQuery(id+"F0.wireOp",EDGE,"E7.11.3"),sQuery(id+"F0.wireOp",EDGE,"E7.11.4"),sQuery(id+"F0.wireOp",EDGE,"E7.12.0"),sQuery(id+"F0.wireOp",EDGE,"E7.12.1"),sQuery(id+"F0.wireOp",EDGE,"E7.12.2"),sQuery(id+"F0.wireOp",EDGE,"E7.12.3"),sQuery(id+"F0.wireOp",EDGE,"E7.12.4"),sQuery(id+"F0.wireOp",EDGE,"E7.13.0"),sQuery(id+"F0.wireOp",EDGE,"E7.13.1"),sQuery(id+"F0.wireOp",EDGE,"E7.13.2"),sQuery(id+"F0.wireOp",EDGE,"E7.13.3"),sQuery(id+"F0.wireOp",EDGE,"E7.13.4"),sQuery(id+"F0.wireOp",EDGE,"E7.14.0"),sQuery(id+"F0.wireOp",EDGE,"E7.14.1"),sQuery(id+"F0.wireOp",EDGE,"E7.14.2"),sQuery(id+"F0.wireOp",EDGE,"E7.14.3"),sQuery(id+"F0.wireOp",EDGE,"E7.14.4"),sQuery(id+"F0.wireOp",EDGE,"E7.15.0"),sQuery(id+"F0.wireOp",EDGE,"E7.15.1"),sQuery(id+"F0.wireOp",EDGE,"E7.15.2"),sQuery(id+"F0.wireOp",EDGE,"E7.15.3"),sQuery(id+"F0.wireOp",EDGE,"E7.15.4"),sQuery(id+"F0.wireOp",EDGE,"E7.16.0"),sQuery(id+"F0.wireOp",EDGE,"E7.16.1"),sQuery(id+"F0.wireOp",EDGE,"E7.16.2"),sQuery(id+"F0.wireOp",EDGE,"E7.16.3"),sQuery(id+"F0.wireOp",EDGE,"E7.16.4"),sQuery(id+"F0.wireOp",EDGE,"E7.17.0"),sQuery(id+"F0.wireOp",EDGE,"E7.17.1"),sQuery(id+"F0.wireOp",EDGE,"E7.17.2"),sQuery(id+"F0.wireOp",EDGE,"E7.17.3"),sQuery(id+"F0.wireOp",EDGE,"E7.17.4"),sQuery(id+"F0.wireOp",EDGE,"E7.18.0"),sQuery(id+"F0.wireOp",EDGE,"E7.18.1"),sQuery(id+"F0.wireOp",EDGE,"E7.18.2"),sQuery(id+"F0.wireOp",EDGE,"E7.18.3"),sQuery(id+"F0.wireOp",EDGE,"E7.18.4"),sQuery(id+"F0.wireOp",EDGE,"E7.19.0"),sQuery(id+"F0.wireOp",EDGE,"E7.19.1"),sQuery(id+"F0.wireOp",EDGE,"E7.19.2"),sQuery(id+"F0.wireOp",EDGE,"E7.19.3"),sQuery(id+"F0.wireOp",EDGE,"E7.19.4"),sQuery(id+"F0.wireOp",EDGE,"E7.20.0"),sQuery(id+"F0.wireOp",EDGE,"E7.20.1"),sQuery(id+"F0.wireOp",EDGE,"E7.20.2"),sQuery(id+"F0.wireOp",EDGE,"E7.20.3"),sQuery(id+"F0.wireOp",EDGE,"E7.20.4"),sQuery(id+"F0.wireOp",EDGE,"E7.21.0"),sQuery(id+"F0.wireOp",EDGE,"E7.21.1"),sQuery(id+"F0.wireOp",EDGE,"E7.21.2"),sQuery(id+"F0.wireOp",EDGE,"E7.21.3"),sQuery(id+"F0.wireOp",EDGE,"E7.21.4"),sQuery(id+"F0.wireOp",EDGE,"E7.22.0"),sQuery(id+"F0.wireOp",EDGE,"E7.22.1"),sQuery(id+"F0.wireOp",EDGE,"E7.22.2"),sQuery(id+"F0.wireOp",EDGE,"E7.22.3"),sQuery(id+"F0.wireOp",EDGE,"E7.22.4"),sQuery(id+"F0.wireOp",EDGE,"E7.23.0"),sQuery(id+"F0.wireOp",EDGE,"E7.23.1"),sQuery(id+"F0.wireOp",EDGE,"E7.23.2"),sQuery(id+"F0.wireOp",EDGE,"E7.23.3"),sQuery(id+"F0.wireOp",EDGE,"E7.23.4"),sQuery(id+"F0.wireOp",EDGE,"E7.24.0"),sQuery(id+"F0.wireOp",EDGE,"E7.24.1"),sQuery(id+"F0.wireOp",EDGE,"E7.24.2"),sQuery(id+"F0.wireOp",EDGE,"E7.24.3"),sQuery(id+"F0.wireOp",EDGE,"E7.24.4"),sQuery(id+"F0.wireOp",EDGE,"E7.25.0"),sQuery(id+"F0.wireOp",EDGE,"E7.25.1"),sQuery(id+"F0.wireOp",EDGE,"E7.25.2"),sQuery(id+"F0.wireOp",EDGE,"E7.25.3"),sQuery(id+"F0.wireOp",EDGE,"E7.25.4"),sQuery(id+"F0.wireOp",EDGE,"E7.26.0"),sQuery(id+"F0.wireOp",EDGE,"E7.26.1"),sQuery(id+"F0.wireOp",EDGE,"E7.26.2"),sQuery(id+"F0.wireOp",EDGE,"E7.26.3"),sQuery(id+"F0.wireOp",EDGE,"E7.26.4"),sQuery(id+"F0.wireOp",EDGE,"E7.27.0"),sQuery(id+"F0.wireOp",EDGE,"E7.27.1"),sQuery(id+"F0.wireOp",EDGE,"E7.27.2"),sQuery(id+"F0.wireOp",EDGE,"E7.27.3"),sQuery(id+"F0.wireOp",EDGE,"E7.27.4"),sQuery(id+"F0.wireOp",EDGE,"E7.28.0"),sQuery(id+"F0.wireOp",EDGE,"E7.28.1"),sQuery(id+"F0.wireOp",EDGE,"E7.28.2"),sQuery(id+"F0.wireOp",EDGE,"E7.28.3"),sQuery(id+"F0.wireOp",EDGE,"E7.28.4"),sQuery(id+"F0.wireOp",EDGE,"E7.29.0"),sQuery(id+"F0.wireOp",EDGE,"E7.29.1"),sQuery(id+"F0.wireOp",EDGE,"E7.29.2"),sQuery(id+"F0.wireOp",EDGE,"E7.29.3"),sQuery(id+"F0.wireOp",EDGE,"E7.29.4"),sQuery(id+"F0.wireOp",EDGE,"E7.30.0"),sQuery(id+"F0.wireOp",EDGE,"E7.30.1"),sQuery(id+"F0.wireOp",EDGE,"E7.30.2"),sQuery(id+"F0.wireOp",EDGE,"E7.30.3"),sQuery(id+"F0.wireOp",EDGE,"E7.30.4"),sQuery(id+"F0.wireOp",EDGE,"E7.31.0"),sQuery(id+"F0.wireOp",EDGE,"E7.31.1"),sQuery(id+"F0.wireOp",EDGE,"E7.31.2"),sQuery(id+"F0.wireOp",EDGE,"E7.31.3"),sQuery(id+"F0.wireOp",EDGE,"E7.31.4"),sQuery(id+"F0.wireOp",EDGE,"E8.trimOffspring"),sQuery(id+"F0.wireOp",EDGE,"E9.trimOffspring"),sQuery(id+"F0.wireOp",EDGE,"E10.trimOffspring"),sQuery(id+"F0.wireOp",EDGE,"E11.trimOffspring"),sQuery(id+"F0.wireOp",EDGE,"E12.trimOffspring"),sQuery(id+"F0.wireOp",EDGE,"E13.trimOffspring"),sQuery(id+"F0.wireOp",EDGE,"E14.trimOffspring"),sQuery(id+"F0.wireOp",EDGE,"E15.trimOffspring"),sQuery(id+"F0.wireOp",EDGE,"E16.trimOffspring"),sQuery(id+"F0.wireOp",EDGE,"E17.trimOffspring"),sQuery(id+"F0.wireOp",EDGE,"E18.trimOffspring"),sQuery(id+"F0.wireOp",EDGE,"E19.trimOffspring"),sQuery(id+"F0.wireOp",EDGE,"E20.trimOffspring"),sQuery(id+"F0.wireOp",EDGE,"E21.trimOffspring"),sQuery(id+"F0.wireOp",EDGE,"E22.trimOffspring"),sQuery(id+"F0.wireOp",EDGE,"E23.trimOffspring"),sQuery(id+"F0.wireOp",EDGE,"E24.trimOffspring"),sQuery(id+"F0.wireOp",EDGE,"E25.trimOffspring"),sQuery(id+"F0.wireOp",EDGE,"E26.trimOffspring"),sQuery(id+"F0.wireOp",EDGE,"E27.trimOffspring"),sQuery(id+"F0.wireOp",EDGE,"E28.trimOffspring"),sQuery(id+"F0.wireOp",EDGE,"E29.trimOffspring"),sQuery(id+"F0.wireOp",EDGE,"E30.trimOffspring"),sQuery(id+"F0.wireOp",EDGE,"E31.trimOffspring"),sQuery(id+"F0.wireOp",EDGE,"E32.trimOffspring"),sQuery(id+"F0.wireOp",EDGE,"E33.trimOffspring"),sQuery(id+"F0.wireOp",EDGE,"E34.trimOffspring"),sQuery(id+"F0.wireOp",EDGE,"E35.trimOffspring"),sQuery(id+"F0.wireOp",EDGE,"E36.trimOffspring"),sQuery(id+"F0.wireOp",EDGE,"E37.trimOffspring"),sQuery(id+"F0.wireOp",EDGE,"E38.trimOffspring")])],"isStart":false});
            var sketch = newSketch(context, id + "F3", { "sketchPlane" : qUnion([Q0])});
            skCircle(sketch, "E39", {"center": v(0, 0) * mm, "radius": 19.05 * mm});
            skLineSegment(sketch, "E40.5.0", {"start": v(-8.87, 4.62) * mm, "end": v(-10.96, 6.72) * mm});
            skLineSegment(sketch, "E40.5.1", {"start": v(-6.72, 10.96) * mm, "end": v(-10.96, 6.72) * mm});
            skLineSegment(sketch, "E40.5.2", {"start": v(-4.62, 8.87) * mm, "end": v(-6.72, 10.96) * mm});
            skArc(sketch, "E41.converted", {"start": v(-8.87, 4.62) * mm, "mid": v(7.07, -7.07) * mm, "end": v(-4.62, 8.87) * mm});
            skPoint(sketch, "E42", {"position": v(-8.84, 8.84) * mm});
            skLineSegment(sketch, "E43", {"start": v(0, 0) * mm, "end": v(-8.84, 8.84) * mm, "construction": true});
            skSolve(sketch);
        }
        {
            var Q0;
            Q0=makeQuery(id+"F3.imprint","IMPRINT",FACE,{"disambiguationData":[TD([[makeQuery(id+"F3.imprint","IMPRINT",EDGE,{"derivedFrom":sQuery(id+"F3.wireOp",EDGE,"E39")}),1.0]])]});
            extrude(context, id + "F4", {"entities" : qUnion([Q0]), "operationType" : NewBodyOperationType.ADD, "depth" : 19.05 * mm, "offsetDistance" : 25.4 * mm, "hasSecondDirection" : true, "secondDirectionOppositeDirection" : true, "secondDirectionDepth" : 31.75 * mm});
        }
        {
            var Q0;
            Q0=makeQuery(id+"F4.boolean.opBoolean","SPLIT",FACE,{"disambiguationData":[TD([makeQuery(id+"F4.opExtrude","SWEPT_FACE",FACE,{"disambiguationData":[OSD([sQuery(id+"F3.wireOp",EDGE,"E40.5.0")])]})])],"derivedFrom":makeQuery(id+"F1.opExtrude","CAP_FACE",FACE,{"disambiguationData":[OSD([sQuery(id+"F0.wireOp",EDGE,"E0"),sQuery(id+"F0.wireOp",EDGE,"E1"),sQuery(id+"F0.wireOp",EDGE,"E3"),sQuery(id+"F0.wireOp",EDGE,"E4"),sQuery(id+"F0.wireOp",EDGE,"E5"),sQuery(id+"F0.wireOp",EDGE,"E6"),sQuery(id+"F0.wireOp",EDGE,"E7.1.0"),sQuery(id+"F0.wireOp",EDGE,"E7.1.1"),sQuery(id+"F0.wireOp",EDGE,"E7.1.2"),sQuery(id+"F0.wireOp",EDGE,"E7.1.3"),sQuery(id+"F0.wireOp",EDGE,"E7.1.4"),sQuery(id+"F0.wireOp",EDGE,"E7.2.0"),sQuery(id+"F0.wireOp",EDGE,"E7.2.1"),sQuery(id+"F0.wireOp",EDGE,"E7.2.2"),sQuery(id+"F0.wireOp",EDGE,"E7.2.3"),sQuery(id+"F0.wireOp",EDGE,"E7.2.4"),sQuery(id+"F0.wireOp",EDGE,"E7.3.0"),sQuery(id+"F0.wireOp",EDGE,"E7.3.1"),sQuery(id+"F0.wireOp",EDGE,"E7.3.2"),sQuery(id+"F0.wireOp",EDGE,"E7.3.3"),sQuery(id+"F0.wireOp",EDGE,"E7.3.4"),sQuery(id+"F0.wireOp",EDGE,"E7.4.0"),sQuery(id+"F0.wireOp",EDGE,"E7.4.1"),sQuery(id+"F0.wireOp",EDGE,"E7.4.2"),sQuery(id+"F0.wireOp",EDGE,"E7.4.3"),sQuery(id+"F0.wireOp",EDGE,"E7.4.4"),sQuery(id+"F0.wireOp",EDGE,"E7.5.0"),sQuery(id+"F0.wireOp",EDGE,"E7.5.1"),sQuery(id+"F0.wireOp",EDGE,"E7.5.2"),sQuery(id+"F0.wireOp",EDGE,"E7.5.3"),sQuery(id+"F0.wireOp",EDGE,"E7.5.4"),sQuery(id+"F0.wireOp",EDGE,"E7.6.0"),sQuery(id+"F0.wireOp",EDGE,"E7.6.1"),sQuery(id+"F0.wireOp",EDGE,"E7.6.2"),sQuery(id+"F0.wireOp",EDGE,"E7.6.3"),sQuery(id+"F0.wireOp",EDGE,"E7.6.4"),sQuery(id+"F0.wireOp",EDGE,"E7.7.0"),sQuery(id+"F0.wireOp",EDGE,"E7.7.1"),sQuery(id+"F0.wireOp",EDGE,"E7.7.2"),sQuery(id+"F0.wireOp",EDGE,"E7.7.3"),sQuery(id+"F0.wireOp",EDGE,"E7.7.4"),sQuery(id+"F0.wireOp",EDGE,"E7.8.0"),sQuery(id+"F0.wireOp",EDGE,"E7.8.1"),sQuery(id+"F0.wireOp",EDGE,"E7.8.2"),sQuery(id+"F0.wireOp",EDGE,"E7.8.3"),sQuery(id+"F0.wireOp",EDGE,"E7.8.4"),sQuery(id+"F0.wireOp",EDGE,"E7.9.0"),sQuery(id+"F0.wireOp",EDGE,"E7.9.1"),sQuery(id+"F0.wireOp",EDGE,"E7.9.2"),sQuery(id+"F0.wireOp",EDGE,"E7.9.3"),sQuery(id+"F0.wireOp",EDGE,"E7.9.4"),sQuery(id+"F0.wireOp",EDGE,"E7.10.0"),sQuery(id+"F0.wireOp",EDGE,"E7.10.1"),sQuery(id+"F0.wireOp",EDGE,"E7.10.2"),sQuery(id+"F0.wireOp",EDGE,"E7.10.3"),sQuery(id+"F0.wireOp",EDGE,"E7.10.4"),sQuery(id+"F0.wireOp",EDGE,"E7.11.0"),sQuery(id+"F0.wireOp",EDGE,"E7.11.1"),sQuery(id+"F0.wireOp",EDGE,"E7.11.2"),sQuery(id+"F0.wireOp",EDGE,"E7.11.3"),sQuery(id+"F0.wireOp",EDGE,"E7.11.4"),sQuery(id+"F0.wireOp",EDGE,"E7.12.0"),sQuery(id+"F0.wireOp",EDGE,"E7.12.1"),sQuery(id+"F0.wireOp",EDGE,"E7.12.2"),sQuery(id+"F0.wireOp",EDGE,"E7.12.3"),sQuery(id+"F0.wireOp",EDGE,"E7.12.4"),sQuery(id+"F0.wireOp",EDGE,"E7.13.0"),sQuery(id+"F0.wireOp",EDGE,"E7.13.1"),sQuery(id+"F0.wireOp",EDGE,"E7.13.2"),sQuery(id+"F0.wireOp",EDGE,"E7.13.3"),sQuery(id+"F0.wireOp",EDGE,"E7.13.4"),sQuery(id+"F0.wireOp",EDGE,"E7.14.0"),sQuery(id+"F0.wireOp",EDGE,"E7.14.1"),sQuery(id+"F0.wireOp",EDGE,"E7.14.2"),sQuery(id+"F0.wireOp",EDGE,"E7.14.3"),sQuery(id+"F0.wireOp",EDGE,"E7.14.4"),sQuery(id+"F0.wireOp",EDGE,"E7.15.0"),sQuery(id+"F0.wireOp",EDGE,"E7.15.1"),sQuery(id+"F0.wireOp",EDGE,"E7.15.2"),sQuery(id+"F0.wireOp",EDGE,"E7.15.3"),sQuery(id+"F0.wireOp",EDGE,"E7.15.4"),sQuery(id+"F0.wireOp",EDGE,"E7.16.0"),sQuery(id+"F0.wireOp",EDGE,"E7.16.1"),sQuery(id+"F0.wireOp",EDGE,"E7.16.2"),sQuery(id+"F0.wireOp",EDGE,"E7.16.3"),sQuery(id+"F0.wireOp",EDGE,"E7.16.4"),sQuery(id+"F0.wireOp",EDGE,"E7.17.0"),sQuery(id+"F0.wireOp",EDGE,"E7.17.1"),sQuery(id+"F0.wireOp",EDGE,"E7.17.2"),sQuery(id+"F0.wireOp",EDGE,"E7.17.3"),sQuery(id+"F0.wireOp",EDGE,"E7.17.4"),sQuery(id+"F0.wireOp",EDGE,"E7.18.0"),sQuery(id+"F0.wireOp",EDGE,"E7.18.1"),sQuery(id+"F0.wireOp",EDGE,"E7.18.2"),sQuery(id+"F0.wireOp",EDGE,"E7.18.3"),sQuery(id+"F0.wireOp",EDGE,"E7.18.4"),sQuery(id+"F0.wireOp",EDGE,"E7.19.0"),sQuery(id+"F0.wireOp",EDGE,"E7.19.1"),sQuery(id+"F0.wireOp",EDGE,"E7.19.2"),sQuery(id+"F0.wireOp",EDGE,"E7.19.3"),sQuery(id+"F0.wireOp",EDGE,"E7.19.4"),sQuery(id+"F0.wireOp",EDGE,"E7.20.0"),sQuery(id+"F0.wireOp",EDGE,"E7.20.1"),sQuery(id+"F0.wireOp",EDGE,"E7.20.2"),sQuery(id+"F0.wireOp",EDGE,"E7.20.3"),sQuery(id+"F0.wireOp",EDGE,"E7.20.4"),sQuery(id+"F0.wireOp",EDGE,"E7.21.0"),sQuery(id+"F0.wireOp",EDGE,"E7.21.1"),sQuery(id+"F0.wireOp",EDGE,"E7.21.2"),sQuery(id+"F0.wireOp",EDGE,"E7.21.3"),sQuery(id+"F0.wireOp",EDGE,"E7.21.4"),sQuery(id+"F0.wireOp",EDGE,"E7.22.0"),sQuery(id+"F0.wireOp",EDGE,"E7.22.1"),sQuery(id+"F0.wireOp",EDGE,"E7.22.2"),sQuery(id+"F0.wireOp",EDGE,"E7.22.3"),sQuery(id+"F0.wireOp",EDGE,"E7.22.4"),sQuery(id+"F0.wireOp",EDGE,"E7.23.0"),sQuery(id+"F0.wireOp",EDGE,"E7.23.1"),sQuery(id+"F0.wireOp",EDGE,"E7.23.2"),sQuery(id+"F0.wireOp",EDGE,"E7.23.3"),sQuery(id+"F0.wireOp",EDGE,"E7.23.4"),sQuery(id+"F0.wireOp",EDGE,"E7.24.0"),sQuery(id+"F0.wireOp",EDGE,"E7.24.1"),sQuery(id+"F0.wireOp",EDGE,"E7.24.2"),sQuery(id+"F0.wireOp",EDGE,"E7.24.3"),sQuery(id+"F0.wireOp",EDGE,"E7.24.4"),sQuery(id+"F0.wireOp",EDGE,"E7.25.0"),sQuery(id+"F0.wireOp",EDGE,"E7.25.1"),sQuery(id+"F0.wireOp",EDGE,"E7.25.2"),sQuery(id+"F0.wireOp",EDGE,"E7.25.3"),sQuery(id+"F0.wireOp",EDGE,"E7.25.4"),sQuery(id+"F0.wireOp",EDGE,"E7.26.0"),sQuery(id+"F0.wireOp",EDGE,"E7.26.1"),sQuery(id+"F0.wireOp",EDGE,"E7.26.2"),sQuery(id+"F0.wireOp",EDGE,"E7.26.3"),sQuery(id+"F0.wireOp",EDGE,"E7.26.4"),sQuery(id+"F0.wireOp",EDGE,"E7.27.0"),sQuery(id+"F0.wireOp",EDGE,"E7.27.1"),sQuery(id+"F0.wireOp",EDGE,"E7.27.2"),sQuery(id+"F0.wireOp",EDGE,"E7.27.3"),sQuery(id+"F0.wireOp",EDGE,"E7.27.4"),sQuery(id+"F0.wireOp",EDGE,"E7.28.0"),sQuery(id+"F0.wireOp",EDGE,"E7.28.1"),sQuery(id+"F0.wireOp",EDGE,"E7.28.2"),sQuery(id+"F0.wireOp",EDGE,"E7.28.3"),sQuery(id+"F0.wireOp",EDGE,"E7.28.4"),sQuery(id+"F0.wireOp",EDGE,"E7.29.0"),sQuery(id+"F0.wireOp",EDGE,"E7.29.1"),sQuery(id+"F0.wireOp",EDGE,"E7.29.2"),sQuery(id+"F0.wireOp",EDGE,"E7.29.3"),sQuery(id+"F0.wireOp",EDGE,"E7.29.4"),sQuery(id+"F0.wireOp",EDGE,"E7.30.0"),sQuery(id+"F0.wireOp",EDGE,"E7.30.1"),sQuery(id+"F0.wireOp",EDGE,"E7.30.2"),sQuery(id+"F0.wireOp",EDGE,"E7.30.3"),sQuery(id+"F0.wireOp",EDGE,"E7.30.4"),sQuery(id+"F0.wireOp",EDGE,"E7.31.0"),sQuery(id+"F0.wireOp",EDGE,"E7.31.1"),sQuery(id+"F0.wireOp",EDGE,"E7.31.2"),sQuery(id+"F0.wireOp",EDGE,"E7.31.3"),sQuery(id+"F0.wireOp",EDGE,"E7.31.4"),sQuery(id+"F0.wireOp",EDGE,"E8.trimOffspring"),sQuery(id+"F0.wireOp",EDGE,"E9.trimOffspring"),sQuery(id+"F0.wireOp",EDGE,"E10.trimOffspring"),sQuery(id+"F0.wireOp",EDGE,"E11.trimOffspring"),sQuery(id+"F0.wireOp",EDGE,"E12.trimOffspring"),sQuery(id+"F0.wireOp",EDGE,"E13.trimOffspring"),sQuery(id+"F0.wireOp",EDGE,"E14.trimOffspring"),sQuery(id+"F0.wireOp",EDGE,"E15.trimOffspring"),sQuery(id+"F0.wireOp",EDGE,"E16.trimOffspring"),sQuery(id+"F0.wireOp",EDGE,"E17.trimOffspring"),sQuery(id+"F0.wireOp",EDGE,"E18.trimOffspring"),sQuery(id+"F0.wireOp",EDGE,"E19.trimOffspring"),sQuery(id+"F0.wireOp",EDGE,"E20.trimOffspring"),sQuery(id+"F0.wireOp",EDGE,"E21.trimOffspring"),sQuery(id+"F0.wireOp",EDGE,"E22.trimOffspring"),sQuery(id+"F0.wireOp",EDGE,"E23.trimOffspring"),sQuery(id+"F0.wireOp",EDGE,"E24.trimOffspring"),sQuery(id+"F0.wireOp",EDGE,"E25.trimOffspring"),sQuery(id+"F0.wireOp",EDGE,"E26.trimOffspring"),sQuery(id+"F0.wireOp",EDGE,"E27.trimOffspring"),sQuery(id+"F0.wireOp",EDGE,"E28.trimOffspring"),sQuery(id+"F0.wireOp",EDGE,"E29.trimOffspring"),sQuery(id+"F0.wireOp",EDGE,"E30.trimOffspring"),sQuery(id+"F0.wireOp",EDGE,"E31.trimOffspring"),sQuery(id+"F0.wireOp",EDGE,"E32.trimOffspring"),sQuery(id+"F0.wireOp",EDGE,"E33.trimOffspring"),sQuery(id+"F0.wireOp",EDGE,"E34.trimOffspring"),sQuery(id+"F0.wireOp",EDGE,"E35.trimOffspring"),sQuery(id+"F0.wireOp",EDGE,"E36.trimOffspring"),sQuery(id+"F0.wireOp",EDGE,"E37.trimOffspring"),sQuery(id+"F0.wireOp",EDGE,"E38.trimOffspring")])],"isStart":true})});
            extrude(context, id + "F5", {"entities" : qUnion([Q0]), "operationType" : NewBodyOperationType.REMOVE, "oppositeDirection" : true, "depth" : 25.4 * mm, "offsetDistance" : 25.4 * mm});
        }
        {
            var Q0;
            Q0=makeQuery(id+"F4.boolean.opBoolean","INTERSECT",EDGE,{"derivedFrom":[makeQuery(id+"F1.opExtrude","CAP_FACE",FACE,{"disambiguationData":[OSD([sQuery(id+"F0.wireOp",EDGE,"E0"),sQuery(id+"F0.wireOp",EDGE,"E1"),sQuery(id+"F0.wireOp",EDGE,"E3"),sQuery(id+"F0.wireOp",EDGE,"E4"),sQuery(id+"F0.wireOp",EDGE,"E5"),sQuery(id+"F0.wireOp",EDGE,"E6"),sQuery(id+"F0.wireOp",EDGE,"E7.1.0"),sQuery(id+"F0.wireOp",EDGE,"E7.1.1"),sQuery(id+"F0.wireOp",EDGE,"E7.1.2"),sQuery(id+"F0.wireOp",EDGE,"E7.1.3"),sQuery(id+"F0.wireOp",EDGE,"E7.1.4"),sQuery(id+"F0.wireOp",EDGE,"E7.2.0"),sQuery(id+"F0.wireOp",EDGE,"E7.2.1"),sQuery(id+"F0.wireOp",EDGE,"E7.2.2"),sQuery(id+"F0.wireOp",EDGE,"E7.2.3"),sQuery(id+"F0.wireOp",EDGE,"E7.2.4"),sQuery(id+"F0.wireOp",EDGE,"E7.3.0"),sQuery(id+"F0.wireOp",EDGE,"E7.3.1"),sQuery(id+"F0.wireOp",EDGE,"E7.3.2"),sQuery(id+"F0.wireOp",EDGE,"E7.3.3"),sQuery(id+"F0.wireOp",EDGE,"E7.3.4"),sQuery(id+"F0.wireOp",EDGE,"E7.4.0"),sQuery(id+"F0.wireOp",EDGE,"E7.4.1"),sQuery(id+"F0.wireOp",EDGE,"E7.4.2"),sQuery(id+"F0.wireOp",EDGE,"E7.4.3"),sQuery(id+"F0.wireOp",EDGE,"E7.4.4"),sQuery(id+"F0.wireOp",EDGE,"E7.5.0"),sQuery(id+"F0.wireOp",EDGE,"E7.5.1"),sQuery(id+"F0.wireOp",EDGE,"E7.5.2"),sQuery(id+"F0.wireOp",EDGE,"E7.5.3"),sQuery(id+"F0.wireOp",EDGE,"E7.5.4"),sQuery(id+"F0.wireOp",EDGE,"E7.6.0"),sQuery(id+"F0.wireOp",EDGE,"E7.6.1"),sQuery(id+"F0.wireOp",EDGE,"E7.6.2"),sQuery(id+"F0.wireOp",EDGE,"E7.6.3"),sQuery(id+"F0.wireOp",EDGE,"E7.6.4"),sQuery(id+"F0.wireOp",EDGE,"E7.7.0"),sQuery(id+"F0.wireOp",EDGE,"E7.7.1"),sQuery(id+"F0.wireOp",EDGE,"E7.7.2"),sQuery(id+"F0.wireOp",EDGE,"E7.7.3"),sQuery(id+"F0.wireOp",EDGE,"E7.7.4"),sQuery(id+"F0.wireOp",EDGE,"E7.8.0"),sQuery(id+"F0.wireOp",EDGE,"E7.8.1"),sQuery(id+"F0.wireOp",EDGE,"E7.8.2"),sQuery(id+"F0.wireOp",EDGE,"E7.8.3"),sQuery(id+"F0.wireOp",EDGE,"E7.8.4"),sQuery(id+"F0.wireOp",EDGE,"E7.9.0"),sQuery(id+"F0.wireOp",EDGE,"E7.9.1"),sQuery(id+"F0.wireOp",EDGE,"E7.9.2"),sQuery(id+"F0.wireOp",EDGE,"E7.9.3"),sQuery(id+"F0.wireOp",EDGE,"E7.9.4"),sQuery(id+"F0.wireOp",EDGE,"E7.10.0"),sQuery(id+"F0.wireOp",EDGE,"E7.10.1"),sQuery(id+"F0.wireOp",EDGE,"E7.10.2"),sQuery(id+"F0.wireOp",EDGE,"E7.10.3"),sQuery(id+"F0.wireOp",EDGE,"E7.10.4"),sQuery(id+"F0.wireOp",EDGE,"E7.11.0"),sQuery(id+"F0.wireOp",EDGE,"E7.11.1"),sQuery(id+"F0.wireOp",EDGE,"E7.11.2"),sQuery(id+"F0.wireOp",EDGE,"E7.11.3"),sQuery(id+"F0.wireOp",EDGE,"E7.11.4"),sQuery(id+"F0.wireOp",EDGE,"E7.12.0"),sQuery(id+"F0.wireOp",EDGE,"E7.12.1"),sQuery(id+"F0.wireOp",EDGE,"E7.12.2"),sQuery(id+"F0.wireOp",EDGE,"E7.12.3"),sQuery(id+"F0.wireOp",EDGE,"E7.12.4"),sQuery(id+"F0.wireOp",EDGE,"E7.13.0"),sQuery(id+"F0.wireOp",EDGE,"E7.13.1"),sQuery(id+"F0.wireOp",EDGE,"E7.13.2"),sQuery(id+"F0.wireOp",EDGE,"E7.13.3"),sQuery(id+"F0.wireOp",EDGE,"E7.13.4"),sQuery(id+"F0.wireOp",EDGE,"E7.14.0"),sQuery(id+"F0.wireOp",EDGE,"E7.14.1"),sQuery(id+"F0.wireOp",EDGE,"E7.14.2"),sQuery(id+"F0.wireOp",EDGE,"E7.14.3"),sQuery(id+"F0.wireOp",EDGE,"E7.14.4"),sQuery(id+"F0.wireOp",EDGE,"E7.15.0"),sQuery(id+"F0.wireOp",EDGE,"E7.15.1"),sQuery(id+"F0.wireOp",EDGE,"E7.15.2"),sQuery(id+"F0.wireOp",EDGE,"E7.15.3"),sQuery(id+"F0.wireOp",EDGE,"E7.15.4"),sQuery(id+"F0.wireOp",EDGE,"E7.16.0"),sQuery(id+"F0.wireOp",EDGE,"E7.16.1"),sQuery(id+"F0.wireOp",EDGE,"E7.16.2"),sQuery(id+"F0.wireOp",EDGE,"E7.16.3"),sQuery(id+"F0.wireOp",EDGE,"E7.16.4"),sQuery(id+"F0.wireOp",EDGE,"E7.17.0"),sQuery(id+"F0.wireOp",EDGE,"E7.17.1"),sQuery(id+"F0.wireOp",EDGE,"E7.17.2"),sQuery(id+"F0.wireOp",EDGE,"E7.17.3"),sQuery(id+"F0.wireOp",EDGE,"E7.17.4"),sQuery(id+"F0.wireOp",EDGE,"E7.18.0"),sQuery(id+"F0.wireOp",EDGE,"E7.18.1"),sQuery(id+"F0.wireOp",EDGE,"E7.18.2"),sQuery(id+"F0.wireOp",EDGE,"E7.18.3"),sQuery(id+"F0.wireOp",EDGE,"E7.18.4"),sQuery(id+"F0.wireOp",EDGE,"E7.19.0"),sQuery(id+"F0.wireOp",EDGE,"E7.19.1"),sQuery(id+"F0.wireOp",EDGE,"E7.19.2"),sQuery(id+"F0.wireOp",EDGE,"E7.19.3"),sQuery(id+"F0.wireOp",EDGE,"E7.19.4"),sQuery(id+"F0.wireOp",EDGE,"E7.20.0"),sQuery(id+"F0.wireOp",EDGE,"E7.20.1"),sQuery(id+"F0.wireOp",EDGE,"E7.20.2"),sQuery(id+"F0.wireOp",EDGE,"E7.20.3"),sQuery(id+"F0.wireOp",EDGE,"E7.20.4"),sQuery(id+"F0.wireOp",EDGE,"E7.21.0"),sQuery(id+"F0.wireOp",EDGE,"E7.21.1"),sQuery(id+"F0.wireOp",EDGE,"E7.21.2"),sQuery(id+"F0.wireOp",EDGE,"E7.21.3"),sQuery(id+"F0.wireOp",EDGE,"E7.21.4"),sQuery(id+"F0.wireOp",EDGE,"E7.22.0"),sQuery(id+"F0.wireOp",EDGE,"E7.22.1"),sQuery(id+"F0.wireOp",EDGE,"E7.22.2"),sQuery(id+"F0.wireOp",EDGE,"E7.22.3"),sQuery(id+"F0.wireOp",EDGE,"E7.22.4"),sQuery(id+"F0.wireOp",EDGE,"E7.23.0"),sQuery(id+"F0.wireOp",EDGE,"E7.23.1"),sQuery(id+"F0.wireOp",EDGE,"E7.23.2"),sQuery(id+"F0.wireOp",EDGE,"E7.23.3"),sQuery(id+"F0.wireOp",EDGE,"E7.23.4"),sQuery(id+"F0.wireOp",EDGE,"E7.24.0"),sQuery(id+"F0.wireOp",EDGE,"E7.24.1"),sQuery(id+"F0.wireOp",EDGE,"E7.24.2"),sQuery(id+"F0.wireOp",EDGE,"E7.24.3"),sQuery(id+"F0.wireOp",EDGE,"E7.24.4"),sQuery(id+"F0.wireOp",EDGE,"E7.25.0"),sQuery(id+"F0.wireOp",EDGE,"E7.25.1"),sQuery(id+"F0.wireOp",EDGE,"E7.25.2"),sQuery(id+"F0.wireOp",EDGE,"E7.25.3"),sQuery(id+"F0.wireOp",EDGE,"E7.25.4"),sQuery(id+"F0.wireOp",EDGE,"E7.26.0"),sQuery(id+"F0.wireOp",EDGE,"E7.26.1"),sQuery(id+"F0.wireOp",EDGE,"E7.26.2"),sQuery(id+"F0.wireOp",EDGE,"E7.26.3"),sQuery(id+"F0.wireOp",EDGE,"E7.26.4"),sQuery(id+"F0.wireOp",EDGE,"E7.27.0"),sQuery(id+"F0.wireOp",EDGE,"E7.27.1"),sQuery(id+"F0.wireOp",EDGE,"E7.27.2"),sQuery(id+"F0.wireOp",EDGE,"E7.27.3"),sQuery(id+"F0.wireOp",EDGE,"E7.27.4"),sQuery(id+"F0.wireOp",EDGE,"E7.28.0"),sQuery(id+"F0.wireOp",EDGE,"E7.28.1"),sQuery(id+"F0.wireOp",EDGE,"E7.28.2"),sQuery(id+"F0.wireOp",EDGE,"E7.28.3"),sQuery(id+"F0.wireOp",EDGE,"E7.28.4"),sQuery(id+"F0.wireOp",EDGE,"E7.29.0"),sQuery(id+"F0.wireOp",EDGE,"E7.29.1"),sQuery(id+"F0.wireOp",EDGE,"E7.29.2"),sQuery(id+"F0.wireOp",EDGE,"E7.29.3"),sQuery(id+"F0.wireOp",EDGE,"E7.29.4"),sQuery(id+"F0.wireOp",EDGE,"E7.30.0"),sQuery(id+"F0.wireOp",EDGE,"E7.30.1"),sQuery(id+"F0.wireOp",EDGE,"E7.30.2"),sQuery(id+"F0.wireOp",EDGE,"E7.30.3"),sQuery(id+"F0.wireOp",EDGE,"E7.30.4"),sQuery(id+"F0.wireOp",EDGE,"E7.31.0"),sQuery(id+"F0.wireOp",EDGE,"E7.31.1"),sQuery(id+"F0.wireOp",EDGE,"E7.31.2"),sQuery(id+"F0.wireOp",EDGE,"E7.31.3"),sQuery(id+"F0.wireOp",EDGE,"E7.31.4"),sQuery(id+"F0.wireOp",EDGE,"E8.trimOffspring"),sQuery(id+"F0.wireOp",EDGE,"E9.trimOffspring"),sQuery(id+"F0.wireOp",EDGE,"E10.trimOffspring"),sQuery(id+"F0.wireOp",EDGE,"E11.trimOffspring"),sQuery(id+"F0.wireOp",EDGE,"E12.trimOffspring"),sQuery(id+"F0.wireOp",EDGE,"E13.trimOffspring"),sQuery(id+"F0.wireOp",EDGE,"E14.trimOffspring"),sQuery(id+"F0.wireOp",EDGE,"E15.trimOffspring"),sQuery(id+"F0.wireOp",EDGE,"E16.trimOffspring"),sQuery(id+"F0.wireOp",EDGE,"E17.trimOffspring"),sQuery(id+"F0.wireOp",EDGE,"E18.trimOffspring"),sQuery(id+"F0.wireOp",EDGE,"E19.trimOffspring"),sQuery(id+"F0.wireOp",EDGE,"E20.trimOffspring"),sQuery(id+"F0.wireOp",EDGE,"E21.trimOffspring"),sQuery(id+"F0.wireOp",EDGE,"E22.trimOffspring"),sQuery(id+"F0.wireOp",EDGE,"E23.trimOffspring"),sQuery(id+"F0.wireOp",EDGE,"E24.trimOffspring"),sQuery(id+"F0.wireOp",EDGE,"E25.trimOffspring"),sQuery(id+"F0.wireOp",EDGE,"E26.trimOffspring"),sQuery(id+"F0.wireOp",EDGE,"E27.trimOffspring"),sQuery(id+"F0.wireOp",EDGE,"E28.trimOffspring"),sQuery(id+"F0.wireOp",EDGE,"E29.trimOffspring"),sQuery(id+"F0.wireOp",EDGE,"E30.trimOffspring"),sQuery(id+"F0.wireOp",EDGE,"E31.trimOffspring"),sQuery(id+"F0.wireOp",EDGE,"E32.trimOffspring"),sQuery(id+"F0.wireOp",EDGE,"E33.trimOffspring"),sQuery(id+"F0.wireOp",EDGE,"E34.trimOffspring"),sQuery(id+"F0.wireOp",EDGE,"E35.trimOffspring"),sQuery(id+"F0.wireOp",EDGE,"E36.trimOffspring"),sQuery(id+"F0.wireOp",EDGE,"E37.trimOffspring"),sQuery(id+"F0.wireOp",EDGE,"E38.trimOffspring")])],"isStart":false}),makeQuery(id+"F4.opExtrude","SWEPT_FACE",FACE,{"disambiguationData":[OSD([sQuery(id+"F3.wireOp",EDGE,"E39")])]})]});
            var Q1;
            Q1=makeQuery(id+"F4.boolean.opBoolean","INTERSECT",EDGE,{"derivedFrom":[makeQuery(id+"F1.opExtrude","CAP_FACE",FACE,{"disambiguationData":[OSD([sQuery(id+"F0.wireOp",EDGE,"E0"),sQuery(id+"F0.wireOp",EDGE,"E1"),sQuery(id+"F0.wireOp",EDGE,"E3"),sQuery(id+"F0.wireOp",EDGE,"E4"),sQuery(id+"F0.wireOp",EDGE,"E5"),sQuery(id+"F0.wireOp",EDGE,"E6"),sQuery(id+"F0.wireOp",EDGE,"E7.1.0"),sQuery(id+"F0.wireOp",EDGE,"E7.1.1"),sQuery(id+"F0.wireOp",EDGE,"E7.1.2"),sQuery(id+"F0.wireOp",EDGE,"E7.1.3"),sQuery(id+"F0.wireOp",EDGE,"E7.1.4"),sQuery(id+"F0.wireOp",EDGE,"E7.2.0"),sQuery(id+"F0.wireOp",EDGE,"E7.2.1"),sQuery(id+"F0.wireOp",EDGE,"E7.2.2"),sQuery(id+"F0.wireOp",EDGE,"E7.2.3"),sQuery(id+"F0.wireOp",EDGE,"E7.2.4"),sQuery(id+"F0.wireOp",EDGE,"E7.3.0"),sQuery(id+"F0.wireOp",EDGE,"E7.3.1"),sQuery(id+"F0.wireOp",EDGE,"E7.3.2"),sQuery(id+"F0.wireOp",EDGE,"E7.3.3"),sQuery(id+"F0.wireOp",EDGE,"E7.3.4"),sQuery(id+"F0.wireOp",EDGE,"E7.4.0"),sQuery(id+"F0.wireOp",EDGE,"E7.4.1"),sQuery(id+"F0.wireOp",EDGE,"E7.4.2"),sQuery(id+"F0.wireOp",EDGE,"E7.4.3"),sQuery(id+"F0.wireOp",EDGE,"E7.4.4"),sQuery(id+"F0.wireOp",EDGE,"E7.5.0"),sQuery(id+"F0.wireOp",EDGE,"E7.5.1"),sQuery(id+"F0.wireOp",EDGE,"E7.5.2"),sQuery(id+"F0.wireOp",EDGE,"E7.5.3"),sQuery(id+"F0.wireOp",EDGE,"E7.5.4"),sQuery(id+"F0.wireOp",EDGE,"E7.6.0"),sQuery(id+"F0.wireOp",EDGE,"E7.6.1"),sQuery(id+"F0.wireOp",EDGE,"E7.6.2"),sQuery(id+"F0.wireOp",EDGE,"E7.6.3"),sQuery(id+"F0.wireOp",EDGE,"E7.6.4"),sQuery(id+"F0.wireOp",EDGE,"E7.7.0"),sQuery(id+"F0.wireOp",EDGE,"E7.7.1"),sQuery(id+"F0.wireOp",EDGE,"E7.7.2"),sQuery(id+"F0.wireOp",EDGE,"E7.7.3"),sQuery(id+"F0.wireOp",EDGE,"E7.7.4"),sQuery(id+"F0.wireOp",EDGE,"E7.8.0"),sQuery(id+"F0.wireOp",EDGE,"E7.8.1"),sQuery(id+"F0.wireOp",EDGE,"E7.8.2"),sQuery(id+"F0.wireOp",EDGE,"E7.8.3"),sQuery(id+"F0.wireOp",EDGE,"E7.8.4"),sQuery(id+"F0.wireOp",EDGE,"E7.9.0"),sQuery(id+"F0.wireOp",EDGE,"E7.9.1"),sQuery(id+"F0.wireOp",EDGE,"E7.9.2"),sQuery(id+"F0.wireOp",EDGE,"E7.9.3"),sQuery(id+"F0.wireOp",EDGE,"E7.9.4"),sQuery(id+"F0.wireOp",EDGE,"E7.10.0"),sQuery(id+"F0.wireOp",EDGE,"E7.10.1"),sQuery(id+"F0.wireOp",EDGE,"E7.10.2"),sQuery(id+"F0.wireOp",EDGE,"E7.10.3"),sQuery(id+"F0.wireOp",EDGE,"E7.10.4"),sQuery(id+"F0.wireOp",EDGE,"E7.11.0"),sQuery(id+"F0.wireOp",EDGE,"E7.11.1"),sQuery(id+"F0.wireOp",EDGE,"E7.11.2"),sQuery(id+"F0.wireOp",EDGE,"E7.11.3"),sQuery(id+"F0.wireOp",EDGE,"E7.11.4"),sQuery(id+"F0.wireOp",EDGE,"E7.12.0"),sQuery(id+"F0.wireOp",EDGE,"E7.12.1"),sQuery(id+"F0.wireOp",EDGE,"E7.12.2"),sQuery(id+"F0.wireOp",EDGE,"E7.12.3"),sQuery(id+"F0.wireOp",EDGE,"E7.12.4"),sQuery(id+"F0.wireOp",EDGE,"E7.13.0"),sQuery(id+"F0.wireOp",EDGE,"E7.13.1"),sQuery(id+"F0.wireOp",EDGE,"E7.13.2"),sQuery(id+"F0.wireOp",EDGE,"E7.13.3"),sQuery(id+"F0.wireOp",EDGE,"E7.13.4"),sQuery(id+"F0.wireOp",EDGE,"E7.14.0"),sQuery(id+"F0.wireOp",EDGE,"E7.14.1"),sQuery(id+"F0.wireOp",EDGE,"E7.14.2"),sQuery(id+"F0.wireOp",EDGE,"E7.14.3"),sQuery(id+"F0.wireOp",EDGE,"E7.14.4"),sQuery(id+"F0.wireOp",EDGE,"E7.15.0"),sQuery(id+"F0.wireOp",EDGE,"E7.15.1"),sQuery(id+"F0.wireOp",EDGE,"E7.15.2"),sQuery(id+"F0.wireOp",EDGE,"E7.15.3"),sQuery(id+"F0.wireOp",EDGE,"E7.15.4"),sQuery(id+"F0.wireOp",EDGE,"E7.16.0"),sQuery(id+"F0.wireOp",EDGE,"E7.16.1"),sQuery(id+"F0.wireOp",EDGE,"E7.16.2"),sQuery(id+"F0.wireOp",EDGE,"E7.16.3"),sQuery(id+"F0.wireOp",EDGE,"E7.16.4"),sQuery(id+"F0.wireOp",EDGE,"E7.17.0"),sQuery(id+"F0.wireOp",EDGE,"E7.17.1"),sQuery(id+"F0.wireOp",EDGE,"E7.17.2"),sQuery(id+"F0.wireOp",EDGE,"E7.17.3"),sQuery(id+"F0.wireOp",EDGE,"E7.17.4"),sQuery(id+"F0.wireOp",EDGE,"E7.18.0"),sQuery(id+"F0.wireOp",EDGE,"E7.18.1"),sQuery(id+"F0.wireOp",EDGE,"E7.18.2"),sQuery(id+"F0.wireOp",EDGE,"E7.18.3"),sQuery(id+"F0.wireOp",EDGE,"E7.18.4"),sQuery(id+"F0.wireOp",EDGE,"E7.19.0"),sQuery(id+"F0.wireOp",EDGE,"E7.19.1"),sQuery(id+"F0.wireOp",EDGE,"E7.19.2"),sQuery(id+"F0.wireOp",EDGE,"E7.19.3"),sQuery(id+"F0.wireOp",EDGE,"E7.19.4"),sQuery(id+"F0.wireOp",EDGE,"E7.20.0"),sQuery(id+"F0.wireOp",EDGE,"E7.20.1"),sQuery(id+"F0.wireOp",EDGE,"E7.20.2"),sQuery(id+"F0.wireOp",EDGE,"E7.20.3"),sQuery(id+"F0.wireOp",EDGE,"E7.20.4"),sQuery(id+"F0.wireOp",EDGE,"E7.21.0"),sQuery(id+"F0.wireOp",EDGE,"E7.21.1"),sQuery(id+"F0.wireOp",EDGE,"E7.21.2"),sQuery(id+"F0.wireOp",EDGE,"E7.21.3"),sQuery(id+"F0.wireOp",EDGE,"E7.21.4"),sQuery(id+"F0.wireOp",EDGE,"E7.22.0"),sQuery(id+"F0.wireOp",EDGE,"E7.22.1"),sQuery(id+"F0.wireOp",EDGE,"E7.22.2"),sQuery(id+"F0.wireOp",EDGE,"E7.22.3"),sQuery(id+"F0.wireOp",EDGE,"E7.22.4"),sQuery(id+"F0.wireOp",EDGE,"E7.23.0"),sQuery(id+"F0.wireOp",EDGE,"E7.23.1"),sQuery(id+"F0.wireOp",EDGE,"E7.23.2"),sQuery(id+"F0.wireOp",EDGE,"E7.23.3"),sQuery(id+"F0.wireOp",EDGE,"E7.23.4"),sQuery(id+"F0.wireOp",EDGE,"E7.24.0"),sQuery(id+"F0.wireOp",EDGE,"E7.24.1"),sQuery(id+"F0.wireOp",EDGE,"E7.24.2"),sQuery(id+"F0.wireOp",EDGE,"E7.24.3"),sQuery(id+"F0.wireOp",EDGE,"E7.24.4"),sQuery(id+"F0.wireOp",EDGE,"E7.25.0"),sQuery(id+"F0.wireOp",EDGE,"E7.25.1"),sQuery(id+"F0.wireOp",EDGE,"E7.25.2"),sQuery(id+"F0.wireOp",EDGE,"E7.25.3"),sQuery(id+"F0.wireOp",EDGE,"E7.25.4"),sQuery(id+"F0.wireOp",EDGE,"E7.26.0"),sQuery(id+"F0.wireOp",EDGE,"E7.26.1"),sQuery(id+"F0.wireOp",EDGE,"E7.26.2"),sQuery(id+"F0.wireOp",EDGE,"E7.26.3"),sQuery(id+"F0.wireOp",EDGE,"E7.26.4"),sQuery(id+"F0.wireOp",EDGE,"E7.27.0"),sQuery(id+"F0.wireOp",EDGE,"E7.27.1"),sQuery(id+"F0.wireOp",EDGE,"E7.27.2"),sQuery(id+"F0.wireOp",EDGE,"E7.27.3"),sQuery(id+"F0.wireOp",EDGE,"E7.27.4"),sQuery(id+"F0.wireOp",EDGE,"E7.28.0"),sQuery(id+"F0.wireOp",EDGE,"E7.28.1"),sQuery(id+"F0.wireOp",EDGE,"E7.28.2"),sQuery(id+"F0.wireOp",EDGE,"E7.28.3"),sQuery(id+"F0.wireOp",EDGE,"E7.28.4"),sQuery(id+"F0.wireOp",EDGE,"E7.29.0"),sQuery(id+"F0.wireOp",EDGE,"E7.29.1"),sQuery(id+"F0.wireOp",EDGE,"E7.29.2"),sQuery(id+"F0.wireOp",EDGE,"E7.29.3"),sQuery(id+"F0.wireOp",EDGE,"E7.29.4"),sQuery(id+"F0.wireOp",EDGE,"E7.30.0"),sQuery(id+"F0.wireOp",EDGE,"E7.30.1"),sQuery(id+"F0.wireOp",EDGE,"E7.30.2"),sQuery(id+"F0.wireOp",EDGE,"E7.30.3"),sQuery(id+"F0.wireOp",EDGE,"E7.30.4"),sQuery(id+"F0.wireOp",EDGE,"E7.31.0"),sQuery(id+"F0.wireOp",EDGE,"E7.31.1"),sQuery(id+"F0.wireOp",EDGE,"E7.31.2"),sQuery(id+"F0.wireOp",EDGE,"E7.31.3"),sQuery(id+"F0.wireOp",EDGE,"E7.31.4"),sQuery(id+"F0.wireOp",EDGE,"E8.trimOffspring"),sQuery(id+"F0.wireOp",EDGE,"E9.trimOffspring"),sQuery(id+"F0.wireOp",EDGE,"E10.trimOffspring"),sQuery(id+"F0.wireOp",EDGE,"E11.trimOffspring"),sQuery(id+"F0.wireOp",EDGE,"E12.trimOffspring"),sQuery(id+"F0.wireOp",EDGE,"E13.trimOffspring"),sQuery(id+"F0.wireOp",EDGE,"E14.trimOffspring"),sQuery(id+"F0.wireOp",EDGE,"E15.trimOffspring"),sQuery(id+"F0.wireOp",EDGE,"E16.trimOffspring"),sQuery(id+"F0.wireOp",EDGE,"E17.trimOffspring"),sQuery(id+"F0.wireOp",EDGE,"E18.trimOffspring"),sQuery(id+"F0.wireOp",EDGE,"E19.trimOffspring"),sQuery(id+"F0.wireOp",EDGE,"E20.trimOffspring"),sQuery(id+"F0.wireOp",EDGE,"E21.trimOffspring"),sQuery(id+"F0.wireOp",EDGE,"E22.trimOffspring"),sQuery(id+"F0.wireOp",EDGE,"E23.trimOffspring"),sQuery(id+"F0.wireOp",EDGE,"E24.trimOffspring"),sQuery(id+"F0.wireOp",EDGE,"E25.trimOffspring"),sQuery(id+"F0.wireOp",EDGE,"E26.trimOffspring"),sQuery(id+"F0.wireOp",EDGE,"E27.trimOffspring"),sQuery(id+"F0.wireOp",EDGE,"E28.trimOffspring"),sQuery(id+"F0.wireOp",EDGE,"E29.trimOffspring"),sQuery(id+"F0.wireOp",EDGE,"E30.trimOffspring"),sQuery(id+"F0.wireOp",EDGE,"E31.trimOffspring"),sQuery(id+"F0.wireOp",EDGE,"E32.trimOffspring"),sQuery(id+"F0.wireOp",EDGE,"E33.trimOffspring"),sQuery(id+"F0.wireOp",EDGE,"E34.trimOffspring"),sQuery(id+"F0.wireOp",EDGE,"E35.trimOffspring"),sQuery(id+"F0.wireOp",EDGE,"E36.trimOffspring"),sQuery(id+"F0.wireOp",EDGE,"E37.trimOffspring"),sQuery(id+"F0.wireOp",EDGE,"E38.trimOffspring")])],"isStart":true}),makeQuery(id+"F4.opExtrude","SWEPT_FACE",FACE,{"disambiguationData":[OSD([sQuery(id+"F3.wireOp",EDGE,"E39")])]})]});
            fillet(context, id + "F6", {"entities" : qUnion([Q0, Q1]), "radius" : 1.9 * mm, "tangentPropagation" : true, "allowEdgeOverflow" : false});
        }
        {
            var Q0;
            Q0=qCreatedBy(makeId("Front.planeOp"),FACE);
            var sketch = newSketch(context, id + "F7", { "sketchPlane" : qUnion([Q0])});
            skCircle(sketch, "E44", {"center": v(0, 19.05) * mm, "radius": 3.18 * mm});
            skSolve(sketch);
        }
        {
            var Q0;
            Q0 = qSketchRegion(id + "F7", true);
            extrude(context, id + "F8", {"entities" : qUnion([Q0]), "operationType" : NewBodyOperationType.REMOVE, "depth" : 25.4 * mm, "offsetDistance" : 25.4 * mm});
        }
        {
            var Q0;
            Q0=qCreatedBy(makeId("Right.planeOp"),FACE);
            var sketch = newSketch(context, id + "F9", { "sketchPlane" : qUnion([Q0])});
            skCircle(sketch, "E45", {"center": v(0, 19.05) * mm, "radius": 3.18 * mm});
            skSolve(sketch);
        }
        {
            var Q0;
            Q0 = qSketchRegion(id + "F9", true);
            extrude(context, id + "F10", {"entities" : qUnion([Q0]), "operationType" : NewBodyOperationType.REMOVE, "depth" : 25.4 * mm, "offsetDistance" : 25.4 * mm});
        }
    });
